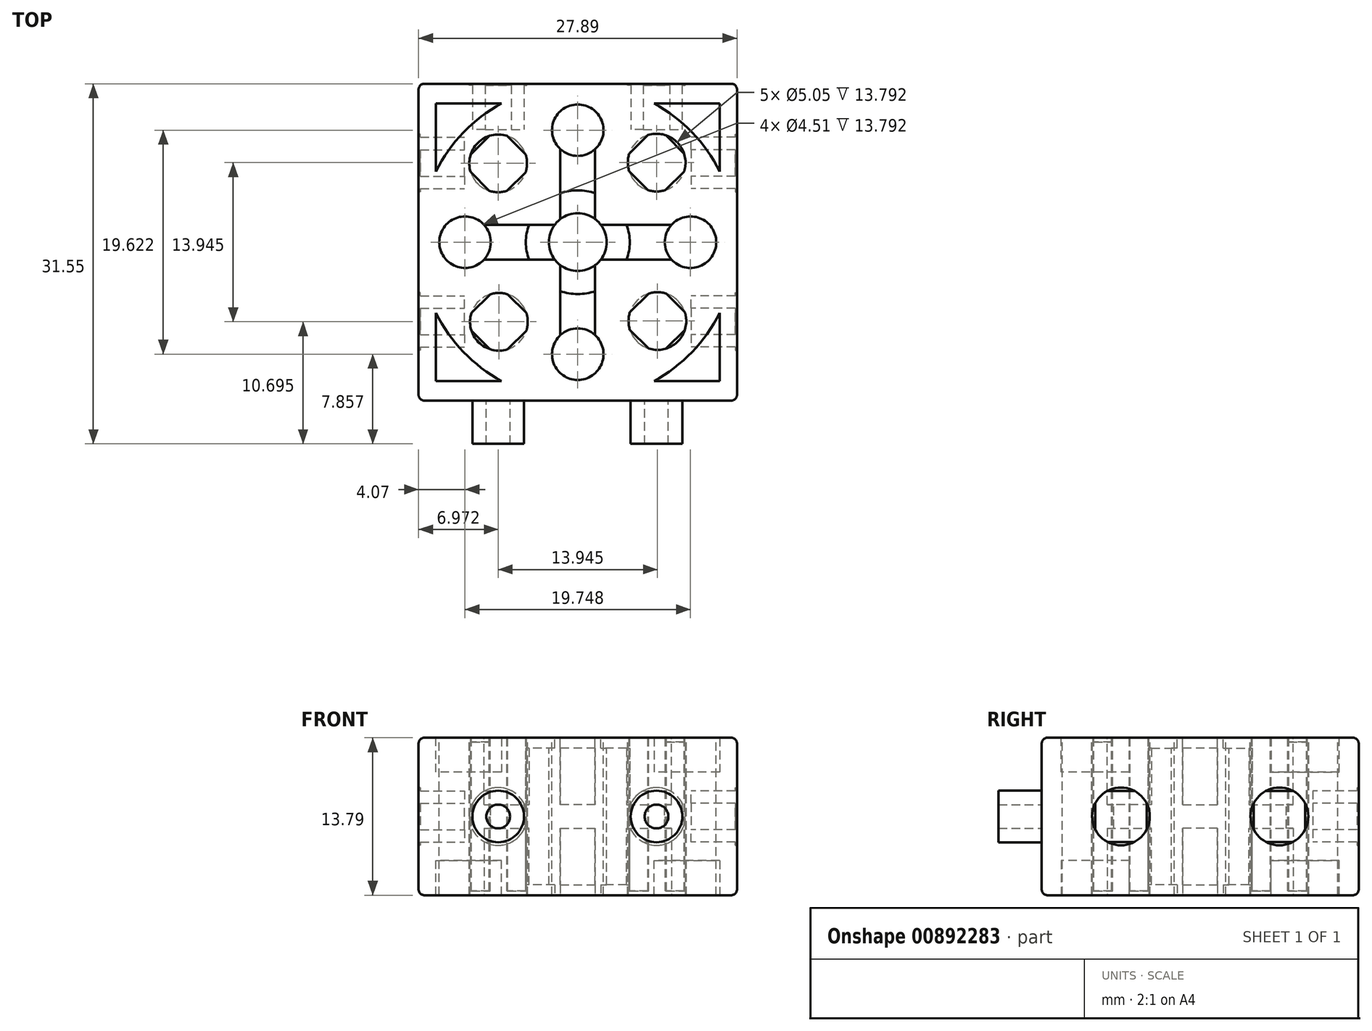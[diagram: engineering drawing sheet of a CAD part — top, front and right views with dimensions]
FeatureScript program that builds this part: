
annotation { "Feature Type Name" : "Feature", "Feature Type Description" : "" }
export const myFeature = defineFeature(function(context is Context, id is Id, definition is map)
    precondition{}
    {
        {
            var Q0;
            Q0=qCreatedBy(makeId("Top.planeOp"),FACE);
            var sketch = newSketch(context, id + "F0", { "sketchPlane" : qUnion([Q0])});
            skLineSegment(sketch, "E0.bottom", {"start": v(-12.61, 9.27) * mm, "end": v(15.28, 9.27) * mm});
            skLineSegment(sketch, "E0.top", {"start": v(-12.61, -18.5) * mm, "end": v(15.28, -18.5) * mm});
            skLineSegment(sketch, "E0.left", {"start": v(-12.61, 9.27) * mm, "end": v(-12.61, -18.5) * mm});
            skLineSegment(sketch, "E0.right", {"start": v(15.28, 9.27) * mm, "end": v(15.28, -18.5) * mm});
            skSolve(sketch);
        }
        {
            var Q0;
            Q0 = qSketchRegion(id + "F0", true);
            extrude(context, id + "F1", {"entities" : qUnion([Q0]), "depth" : 13.8 * mm, "offsetDistance" : 25.4 * mm});
        }
        {
            var Q0;
            Q0=makeQuery(id+"F1.opExtrude","CAP_FACE",FACE,{"disambiguationData":[OSD([sQuery(id+"F0.wireOp",EDGE,"E0.bottom"),sQuery(id+"F0.wireOp",EDGE,"E0.top"),sQuery(id+"F0.wireOp",EDGE,"E0.left"),sQuery(id+"F0.wireOp",EDGE,"E0.right")])],"isStart":false});
            var sketch = newSketch(context, id + "F2", { "sketchPlane" : qUnion([Q0])});
            skLineSegment(sketch, "E1", {"start": v(1.33, 9.27) * mm, "end": v(1.33, -18.5) * mm, "construction": true});
            skLineSegment(sketch, "E2", {"start": v(-12.61, -4.61) * mm, "end": v(15.28, -4.61) * mm, "construction": true});
            skLineSegment(sketch, "E3.bottom", {"start": v(13.75, 7.56) * mm, "end": v(-11.09, 7.56) * mm});
            skLineSegment(sketch, "E3.top", {"start": v(13.75, -16.78) * mm, "end": v(-11.09, -16.78) * mm});
            skLineSegment(sketch, "E3.left", {"start": v(13.75, 7.56) * mm, "end": v(13.75, -16.78) * mm});
            skLineSegment(sketch, "E3.right", {"start": v(-11.09, 7.56) * mm, "end": v(-11.09, -16.78) * mm});
            skPoint(sketch, "E3.middle", {"position": v(1.33, -4.61) * mm});
            skSolve(sketch);
        }
        {
            var Q0;
            Q0 = qSketchRegion(id + "F2", true);
            extrude(context, id + "F3", {"entities" : qUnion([Q0]), "operationType" : NewBodyOperationType.REMOVE, "oppositeDirection" : true, "depth" : 3.02 * mm, "offsetDistance" : 25.4 * mm});
        }
        {
            var Q0;
            Q0=makeQuery(id+"F1.opExtrude","CAP_FACE",FACE,{"disambiguationData":[OSD([sQuery(id+"F0.wireOp",EDGE,"E0.bottom"),sQuery(id+"F0.wireOp",EDGE,"E0.top"),sQuery(id+"F0.wireOp",EDGE,"E0.left"),sQuery(id+"F0.wireOp",EDGE,"E0.right")])],"isStart":true});
            var sketch = newSketch(context, id + "F4", { "sketchPlane" : qUnion([Q0])});
            skLineSegment(sketch, "E4.bottom", {"start": v(-11.09, -7.56) * mm, "end": v(13.75, -7.56) * mm});
            skLineSegment(sketch, "E4.top", {"start": v(-11.09, 16.78) * mm, "end": v(13.75, 16.78) * mm});
            skLineSegment(sketch, "E4.left", {"start": v(-11.09, -7.56) * mm, "end": v(-11.09, 16.78) * mm});
            skLineSegment(sketch, "E4.right", {"start": v(13.75, -7.56) * mm, "end": v(13.75, 16.78) * mm});
            skSolve(sketch);
        }
        {
            var Q0;
            Q0=makeQuery(id+"F4.imprint","IMPRINT",FACE,{"disambiguationData":[TD([[makeQuery(id+"F4.imprint","IMPRINT",EDGE,{"derivedFrom":sQuery(id+"F4.wireOp",EDGE,"E4.bottom")}),1.0]])]});
            extrude(context, id + "F5", {"entities" : qUnion([Q0]), "operationType" : NewBodyOperationType.REMOVE, "oppositeDirection" : true, "depth" : 3.02 * mm, "offsetDistance" : 25.4 * mm});
        }
        {
            var Q0;
            Q0=makeQuery(id+"F5.boolean.opBoolean","COPY",FACE,{"derivedFrom":makeQuery(id+"F5.opExtrude","CAP_FACE",FACE,{"disambiguationData":[OSD([sQuery(id+"F4.wireOp",EDGE,"E4.bottom"),sQuery(id+"F4.wireOp",EDGE,"E4.top"),sQuery(id+"F4.wireOp",EDGE,"E4.left"),sQuery(id+"F4.wireOp",EDGE,"E4.right")])],"isStart":false})});
            var sketch = newSketch(context, id + "F6", { "sketchPlane" : qUnion([Q0])});
            skCircle(sketch, "E5", {"center": v(1.33, 4.61) * mm, "radius": 13.88 * mm});
            skLineSegment(sketch, "E6", {"start": v(1.33, -7.56) * mm, "end": v(1.33, 16.78) * mm, "construction": true});
            skPoint(sketch, "E6.startSnap0", {"position": v(1.33, -7.56) * mm});
            skSolve(sketch);
        }
        {
            var Q0;
            {var subQ0=sQuery(id+"F6.wireOp",EDGE,"E5");var subQ1=makeQuery(id+"F5.boolean.opBoolean","COPY",EDGE,{"derivedFrom":makeQuery(id+"F5.opExtrude","CAP_EDGE",EDGE,{"disambiguationData":[OSD([sQuery(id+"F4.wireOp",EDGE,"E4.top")])],"isStart":false})});var subQ2=makeQuery(id+"F6.imprint","INTERSECT",VERTEX,{"disambiguationData":[OD(0.0)],"derivedFrom":[subQ1,subQ0]});Q0=makeQuery(id+"F6.imprint","IMPRINT",FACE,{"disambiguationData":[TD([[makeQuery(id+"F6.imprint","IMPRINT",EDGE,{"disambiguationData":[TD([[subQ2,-1.0]])],"derivedFrom":subQ0}),1.0]])]});}
            var Q1;
            {var subQ0=sQuery(id+"F6.wireOp",EDGE,"E5");var subQ1=makeQuery(id+"F5.boolean.opBoolean","COPY",EDGE,{"derivedFrom":makeQuery(id+"F5.opExtrude","CAP_EDGE",EDGE,{"disambiguationData":[OSD([sQuery(id+"F4.wireOp",EDGE,"E4.left")])],"isStart":false})});var subQ2=makeQuery(id+"F6.imprint","INTERSECT",VERTEX,{"disambiguationData":[OD(0.0)],"derivedFrom":[subQ1,subQ0]});Q1=makeQuery(id+"F6.imprint","IMPRINT",FACE,{"disambiguationData":[TD([[makeQuery(id+"F6.imprint","IMPRINT",EDGE,{"disambiguationData":[TD([[subQ2,-1.0]])],"derivedFrom":subQ0}),1.0]])]});}
            var Q2;
            {var subQ0=sQuery(id+"F6.wireOp",EDGE,"E5");var subQ1=makeQuery(id+"F5.boolean.opBoolean","COPY",EDGE,{"derivedFrom":makeQuery(id+"F5.opExtrude","CAP_EDGE",EDGE,{"disambiguationData":[OSD([sQuery(id+"F4.wireOp",EDGE,"E4.bottom")])],"isStart":false})});var subQ2=makeQuery(id+"F6.imprint","INTERSECT",VERTEX,{"disambiguationData":[OD(0.0)],"derivedFrom":[subQ1,subQ0]});Q2=makeQuery(id+"F6.imprint","IMPRINT",FACE,{"disambiguationData":[TD([[makeQuery(id+"F6.imprint","IMPRINT",EDGE,{"disambiguationData":[TD([[subQ2,-1.0]])],"derivedFrom":subQ0}),1.0]])]});}
            var Q3;
            {var subQ0=sQuery(id+"F6.wireOp",EDGE,"E5");var subQ1=makeQuery(id+"F5.boolean.opBoolean","COPY",EDGE,{"derivedFrom":makeQuery(id+"F5.opExtrude","CAP_EDGE",EDGE,{"disambiguationData":[OSD([sQuery(id+"F4.wireOp",EDGE,"E4.right")])],"isStart":false})});var subQ2=makeQuery(id+"F6.imprint","INTERSECT",VERTEX,{"disambiguationData":[OD(0.0)],"derivedFrom":[subQ1,subQ0]});Q3=makeQuery(id+"F6.imprint","IMPRINT",FACE,{"disambiguationData":[TD([[makeQuery(id+"F6.imprint","IMPRINT",EDGE,{"disambiguationData":[TD([[subQ2,1.0]])],"derivedFrom":subQ0}),1.0]])]});}
            var Q4;
            {var subQ0=sQuery(id+"F6.wireOp",EDGE,"E5");var subQ8=makeQuery(id+"F5.boolean.opBoolean","COPY",EDGE,{"derivedFrom":makeQuery(id+"F5.opExtrude","CAP_EDGE",EDGE,{"disambiguationData":[OSD([sQuery(id+"F4.wireOp",EDGE,"E4.top")])],"isStart":false})});var subQ11=makeQuery(id+"F6.imprint","INTERSECT",VERTEX,{"disambiguationData":[OD(0.0)],"derivedFrom":[subQ8,subQ0]});Q4=makeQuery(id+"F6.imprint","IMPRINT",FACE,{"disambiguationData":[TD([[makeQuery(id+"F6.imprint","IMPRINT",EDGE,{"disambiguationData":[TD([[subQ11,1.0]])],"derivedFrom":subQ0}),1.0]])]});}
            extrude(context, id + "F7", {"entities" : qUnion([Q0, Q1, Q2, Q3, Q4]), "operationType" : NewBodyOperationType.ADD, "depth" : 3.02 * mm, "offsetDistance" : 25.4 * mm});
        }
        {
            var Q0;
            Q0=makeQuery(id+"F3.boolean.opBoolean","COPY",FACE,{"derivedFrom":makeQuery(id+"F3.opExtrude","CAP_FACE",FACE,{"disambiguationData":[OSD([sQuery(id+"F2.wireOp",EDGE,"E3.bottom"),sQuery(id+"F2.wireOp",EDGE,"E3.top"),sQuery(id+"F2.wireOp",EDGE,"E3.left"),sQuery(id+"F2.wireOp",EDGE,"E3.right")])],"isStart":false})});
            var sketch = newSketch(context, id + "F8", { "sketchPlane" : qUnion([Q0])});
            skLineSegment(sketch, "E7", {"start": v(1.33, 7.56) * mm, "end": v(1.33, -16.78) * mm, "construction": true});
            skCircle(sketch, "E8", {"center": v(1.33, -4.61) * mm, "radius": 13.88 * mm});
            skSolve(sketch);
        }
        {
            var Q0;
            Q0 = qSketchRegion(id + "F8", true);
            extrude(context, id + "F9", {"entities" : qUnion([Q0]), "operationType" : NewBodyOperationType.ADD, "depth" : 3.02 * mm, "offsetDistance" : 25.4 * mm});
        }
        {
            var Q0;
            Q0=makeQuery(id+"F9.boolean.opBoolean","MERGE",FACE,{"derivedFrom":[makeQuery(id+"F1.opExtrude","CAP_FACE",FACE,{"disambiguationData":[OSD([sQuery(id+"F0.wireOp",EDGE,"E0.bottom"),sQuery(id+"F0.wireOp",EDGE,"E0.top"),sQuery(id+"F0.wireOp",EDGE,"E0.left"),sQuery(id+"F0.wireOp",EDGE,"E0.right")])],"isStart":false}),makeQuery(id+"F9.opExtrude","CAP_FACE",FACE,{"disambiguationData":[OSD([sQuery(id+"F8.wireOp",EDGE,"E8")])],"isStart":false})]});
            var sketch = newSketch(context, id + "F10", { "sketchPlane" : qUnion([Q0])});
            skLineSegment(sketch, "E9", {"start": v(-12.61, -4.61) * mm, "end": v(15.28, -4.61) * mm, "construction": true});
            skLineSegment(sketch, "E10", {"start": v(1.33, 9.27) * mm, "end": v(1.33, -18.5) * mm, "construction": true});
            skCircle(sketch, "E11", {"center": v(1.33, -4.61) * mm, "radius": 2.53 * mm});
            skCircle(sketch, "E12", {"center": v(1.33, -14.42) * mm, "radius": 2.25 * mm});
            skCircle(sketch, "E13", {"center": v(1.33, 5.2) * mm, "radius": 2.25 * mm});
            skCircle(sketch, "E14", {"center": v(-8.54, -4.61) * mm, "radius": 2.25 * mm});
            skCircle(sketch, "E15", {"center": v(11.2, -4.61) * mm, "radius": 2.25 * mm});
            skCircle(sketch, "E16", {"center": v(-5.64, 2.3) * mm, "radius": 2.53 * mm});
            skCircle(sketch, "E17.1.0", {"center": v(-5.57, -11.58) * mm, "radius": 2.53 * mm});
            skCircle(sketch, "E17.2.0", {"center": v(8.3, -11.52) * mm, "radius": 2.53 * mm});
            skCircle(sketch, "E17.3.0", {"center": v(8.24, 2.36) * mm, "radius": 2.53 * mm});
            skSolve(sketch);
        }
        {
            var Q0;
            Q0 = qSketchRegion(id + "F10", true);
            extrude(context, id + "F11", {"entities" : qUnion([Q0]), "operationType" : NewBodyOperationType.REMOVE, "oppositeDirection" : true, "depth" : 25.4 * mm, "offsetDistance" : 25.4 * mm});
        }
        {
            var Q0;
            Q0=makeQuery(id+"F9.boolean.opBoolean","MERGE",FACE,{"derivedFrom":[makeQuery(id+"F1.opExtrude","CAP_FACE",FACE,{"disambiguationData":[OSD([sQuery(id+"F0.wireOp",EDGE,"E0.bottom"),sQuery(id+"F0.wireOp",EDGE,"E0.top"),sQuery(id+"F0.wireOp",EDGE,"E0.left"),sQuery(id+"F0.wireOp",EDGE,"E0.right")])],"isStart":false}),makeQuery(id+"F9.opExtrude","CAP_FACE",FACE,{"disambiguationData":[OSD([sQuery(id+"F8.wireOp",EDGE,"E8")])],"isStart":false})]});
            var sketch = newSketch(context, id + "F12", { "sketchPlane" : qUnion([Q0])});
            skLineSegment(sketch, "E18", {"start": v(-12.61, -4.61) * mm, "end": v(15.28, -4.61) * mm, "construction": true});
            skLineSegment(sketch, "E19", {"start": v(1.33, 9.27) * mm, "end": v(1.33, -18.5) * mm, "construction": true});
            skLineSegment(sketch, "E20", {"start": v(-6.88, -3.09) * mm, "end": v(9.55, -3.09) * mm});
            skLineSegment(sketch, "E21", {"start": v(-6.88, -6.14) * mm, "end": v(9.55, -6.14) * mm});
            skLineSegment(sketch, "E22", {"start": v(-0.19, 3.54) * mm, "end": v(-0.19, -12.76) * mm});
            skLineSegment(sketch, "E23", {"start": v(2.86, -12.76) * mm, "end": v(2.86, 3.54) * mm});
            skLineSegment(sketch, "E24", {"start": v(-0.19, -7.96) * mm, "end": v(2.86, -7.96) * mm, "construction": true});
            skPoint(sketch, "E25", {"position": v(1.33, -7.96) * mm});
            skLineSegment(sketch, "E26", {"start": v(-2, -3.09) * mm, "end": v(-2, -6.14) * mm, "construction": true});
            skPoint(sketch, "E27", {"position": v(-2, -4.61) * mm});
            skSolve(sketch);
        }
        {
            var Q0;
            {var subQ0=sQuery(id+"F12.wireOp",EDGE,"E22");var subQ1=makeQuery(id+"F11.boolean.opBoolean","COPY",EDGE,{"derivedFrom":makeQuery(id+"F11.opExtrude","CAP_EDGE",EDGE,{"disambiguationData":[OSD([sQuery(id+"F10.wireOp",EDGE,"E13")])],"isStart":true})});var subQ2=makeQuery(id+"F12.imprint","INTERSECT",VERTEX,{"derivedFrom":[subQ1,subQ0]});Q0=makeQuery(id+"F12.imprint","IMPRINT",FACE,{"disambiguationData":[TD([[makeQuery(id+"F12.imprint","IMPRINT",EDGE,{"disambiguationData":[TD([[subQ2,-1.0]])],"derivedFrom":subQ0}),1.0]])]});}
            var Q1;
            {var subQ0=sQuery(id+"F12.wireOp",EDGE,"E22");var subQ1=makeQuery(id+"F11.boolean.opBoolean","COPY",EDGE,{"derivedFrom":makeQuery(id+"F11.opExtrude","CAP_EDGE",EDGE,{"disambiguationData":[OSD([sQuery(id+"F10.wireOp",EDGE,"E12")])],"isStart":true})});var subQ2=makeQuery(id+"F12.imprint","INTERSECT",VERTEX,{"derivedFrom":[subQ1,subQ0]});Q1=makeQuery(id+"F12.imprint","IMPRINT",FACE,{"disambiguationData":[TD([[makeQuery(id+"F12.imprint","IMPRINT",EDGE,{"disambiguationData":[TD([[subQ2,1.0]])],"derivedFrom":subQ0}),1.0]])]});}
            var Q2;
            {var subQ0=sQuery(id+"F12.wireOp",EDGE,"E20");var subQ1=makeQuery(id+"F11.boolean.opBoolean","COPY",EDGE,{"derivedFrom":makeQuery(id+"F11.opExtrude","CAP_EDGE",EDGE,{"disambiguationData":[OSD([sQuery(id+"F10.wireOp",EDGE,"E14")])],"isStart":true})});var subQ2=makeQuery(id+"F12.imprint","INTERSECT",VERTEX,{"derivedFrom":[subQ1,subQ0]});Q2=makeQuery(id+"F12.imprint","IMPRINT",FACE,{"disambiguationData":[TD([[makeQuery(id+"F12.imprint","IMPRINT",EDGE,{"disambiguationData":[TD([[subQ2,-1.0]])],"derivedFrom":subQ0}),-1.0]])]});}
            var Q3;
            {var subQ0=sQuery(id+"F12.wireOp",EDGE,"E20");var subQ1=makeQuery(id+"F11.boolean.opBoolean","COPY",EDGE,{"derivedFrom":makeQuery(id+"F11.opExtrude","CAP_EDGE",EDGE,{"disambiguationData":[OSD([sQuery(id+"F10.wireOp",EDGE,"E15")])],"isStart":true})});var subQ2=makeQuery(id+"F12.imprint","INTERSECT",VERTEX,{"derivedFrom":[subQ1,subQ0]});Q3=makeQuery(id+"F12.imprint","IMPRINT",FACE,{"disambiguationData":[TD([[makeQuery(id+"F12.imprint","IMPRINT",EDGE,{"disambiguationData":[TD([[subQ2,1.0]])],"derivedFrom":subQ0}),-1.0]])]});}
            extrude(context, id + "F13", {"entities" : qUnion([Q0, Q1, Q2, Q3]), "operationType" : NewBodyOperationType.REMOVE, "oppositeDirection" : true, "depth" : 5.87 * mm, "offsetDistance" : 25.4 * mm});
        }
        {
            var Q0;
            Q0=makeQuery(id+"F7.boolean.opBoolean","MERGE",FACE,{"derivedFrom":[makeQuery(id+"F1.opExtrude","CAP_FACE",FACE,{"disambiguationData":[OSD([sQuery(id+"F0.wireOp",EDGE,"E0.bottom"),sQuery(id+"F0.wireOp",EDGE,"E0.top"),sQuery(id+"F0.wireOp",EDGE,"E0.left"),sQuery(id+"F0.wireOp",EDGE,"E0.right")])],"isStart":true}),makeQuery(id+"F7.opExtrude","CAP_FACE",FACE,{"disambiguationData":[OSD([sQuery(id+"F6.wireOp",EDGE,"E5")])],"isStart":false})]});
            var sketch = newSketch(context, id + "F14", { "sketchPlane" : qUnion([Q0])});
            skLineSegment(sketch, "E28.0", {"start": v(2.86, 12.76) * mm, "end": v(2.86, 6.63) * mm});
            skLineSegment(sketch, "E28.1", {"start": v(3.35, 6.14) * mm, "end": v(9.55, 6.14) * mm});
            skLineSegment(sketch, "E28.2", {"start": v(3.35, 3.09) * mm, "end": v(9.55, 3.09) * mm});
            skLineSegment(sketch, "E28.3", {"start": v(2.86, 2.6) * mm, "end": v(2.86, -3.54) * mm});
            skLineSegment(sketch, "E28.4", {"start": v(-0.19, -3.54) * mm, "end": v(-0.19, 2.6) * mm});
            skLineSegment(sketch, "E28.5", {"start": v(-0.19, 6.63) * mm, "end": v(-0.19, 12.76) * mm});
            skLineSegment(sketch, "E28.6", {"start": v(-6.88, 6.14) * mm, "end": v(-0.68, 6.14) * mm});
            skLineSegment(sketch, "E28.7", {"start": v(-6.88, 3.09) * mm, "end": v(-0.68, 3.09) * mm});
            skSolve(sketch);
        }
        {
            var Q0;
            {var subQ0=sQuery(id+"F14.wireOp",EDGE,"E28.6");Q0=makeQuery(id+"F14.imprint","IMPRINT",FACE,{"disambiguationData":[TD([[makeQuery(id+"F14.imprint","IMPRINT",EDGE,{"derivedFrom":subQ0}),-1.0]])]});}
            var Q1;
            {var subQ0=sQuery(id+"F14.wireOp",EDGE,"E28.3");Q1=makeQuery(id+"F14.imprint","IMPRINT",FACE,{"disambiguationData":[TD([[makeQuery(id+"F14.imprint","IMPRINT",EDGE,{"derivedFrom":subQ0}),-1.0]])]});}
            var Q2;
            {var subQ0=sQuery(id+"F14.wireOp",EDGE,"E28.0");Q2=makeQuery(id+"F14.imprint","IMPRINT",FACE,{"disambiguationData":[TD([[makeQuery(id+"F14.imprint","IMPRINT",EDGE,{"derivedFrom":subQ0}),-1.0]])]});}
            var Q3;
            {var subQ0=sQuery(id+"F14.wireOp",EDGE,"E28.1");Q3=makeQuery(id+"F14.imprint","IMPRINT",FACE,{"disambiguationData":[TD([[makeQuery(id+"F14.imprint","IMPRINT",EDGE,{"derivedFrom":subQ0}),-1.0]])]});}
            extrude(context, id + "F15", {"entities" : qUnion([Q0, Q1, Q2, Q3]), "operationType" : NewBodyOperationType.REMOVE, "oppositeDirection" : true, "depth" : 5.87 * mm, "offsetDistance" : 25.4 * mm});
        }
        {
            var Q0;
            Q0=makeQuery(id+"F15.boolean.opBoolean","COPY",FACE,{"derivedFrom":makeQuery(id+"F15.opExtrude","CAP_FACE",FACE,{"disambiguationData":[OSD([sQuery(id+"F0.wireOp",EDGE,"E0.bottom"),sQuery(id+"F0.wireOp",EDGE,"E0.top"),sQuery(id+"F0.wireOp",EDGE,"E0.left"),sQuery(id+"F0.wireOp",EDGE,"E0.right"),sQuery(id+"F6.wireOp",EDGE,"E5"),sQuery(id+"F10.wireOp",EDGE,"E11"),sQuery(id+"F10.wireOp",EDGE,"E13"),sQuery(id+"F14.wireOp",EDGE,"E28.3"),sQuery(id+"F14.wireOp",EDGE,"E28.4")])],"isStart":false})});
            var sketch = newSketch(context, id + "F16", { "sketchPlane" : qUnion([Q0])});
            skCircle(sketch, "E29", {"center": v(1.33, 4.61) * mm, "radius": 4.55 * mm});
            skCircle(sketch, "E30", {"center": v(1.33, 4.61) * mm, "radius": 2.53 * mm});
            skSolve(sketch);
        }
        {
            var Q0;
            {var subQ5=sQuery(id+"F16.wireOp",EDGE,"E30");Q0=makeQuery(id+"F16.imprint","IMPRINT",FACE,{"disambiguationData":[TD([[makeQuery(id+"F16.imprint","IMPRINT",EDGE,{"disambiguationData":[OD(1.0)],"derivedFrom":subQ5}),-1.0]])]});}
            var Q1;
            {var subQ5=sQuery(id+"F16.wireOp",EDGE,"E30");Q1=makeQuery(id+"F16.imprint","IMPRINT",FACE,{"disambiguationData":[TD([[makeQuery(id+"F16.imprint","IMPRINT",EDGE,{"disambiguationData":[OD(0.0)],"derivedFrom":subQ5}),1.0]])]});}
            extrude(context, id + "F17", {"entities" : qUnion([Q0, Q1]), "operationType" : NewBodyOperationType.ADD, "depth" : 4.95 * mm, "offsetDistance" : 25.4 * mm});
        }
        {
            var Q0;
            Q0=makeQuery(id+"F13.boolean.opBoolean","COPY",FACE,{"derivedFrom":makeQuery(id+"F13.opExtrude","CAP_FACE",FACE,{"disambiguationData":[OSD([sQuery(id+"F10.wireOp",EDGE,"E11"),sQuery(id+"F10.wireOp",EDGE,"E12"),sQuery(id+"F12.wireOp",EDGE,"E22"),sQuery(id+"F12.wireOp",EDGE,"E23")])],"isStart":false})});
            var sketch = newSketch(context, id + "F18", { "sketchPlane" : qUnion([Q0])});
            skCircle(sketch, "E31", {"center": v(1.33, -4.61) * mm, "radius": 4.55 * mm});
            skCircle(sketch, "E32", {"center": v(1.33, -4.61) * mm, "radius": 2.53 * mm});
            skSolve(sketch);
        }
        {
            var Q0;
            {var subQ0=sQuery(id+"F18.wireOp",EDGE,"E31");var subQ1=sQuery(id+"F12.wireOp",EDGE,"E22");var subQ2=makeQuery(id+"F11.boolean.opBoolean","COPY",EDGE,{"derivedFrom":makeQuery(id+"F11.opExtrude","CAP_EDGE",EDGE,{"disambiguationData":[OSD([sQuery(id+"F10.wireOp",EDGE,"E12")])],"isStart":true})});var subQ4=makeQuery(id+"F13.boolean.opBoolean","COPY",EDGE,{"derivedFrom":makeQuery(id+"F13.opExtrude","CAP_EDGE",EDGE,{"disambiguationData":[OSD([subQ1]),TDD([makeQuery(id+"F12.imprint","IMPRINT",EDGE,{"disambiguationData":[TD([[makeQuery(id+"F12.imprint","INTERSECT",VERTEX,{"derivedFrom":[subQ2,subQ1]}),1.0]])],"derivedFrom":subQ1})])],"isStart":false})});var subQ5=makeQuery(id+"F18.imprint","INTERSECT",VERTEX,{"derivedFrom":[subQ4,subQ0]});Q0=makeQuery(id+"F18.imprint","IMPRINT",FACE,{"disambiguationData":[TD([[makeQuery(id+"F18.imprint","IMPRINT",EDGE,{"disambiguationData":[TD([[subQ5,1.0]])],"derivedFrom":subQ0}),1.0]])]});}
            var Q1;
            {var subQ0=sQuery(id+"F18.wireOp",EDGE,"E31");var subQ1=sQuery(id+"F12.wireOp",EDGE,"E22");var subQ2=makeQuery(id+"F11.boolean.opBoolean","COPY",EDGE,{"derivedFrom":makeQuery(id+"F11.opExtrude","CAP_EDGE",EDGE,{"disambiguationData":[OSD([sQuery(id+"F10.wireOp",EDGE,"E12")])],"isStart":true})});var subQ4=makeQuery(id+"F13.boolean.opBoolean","COPY",EDGE,{"derivedFrom":makeQuery(id+"F13.opExtrude","CAP_EDGE",EDGE,{"disambiguationData":[OSD([subQ1]),TDD([makeQuery(id+"F12.imprint","IMPRINT",EDGE,{"disambiguationData":[TD([[makeQuery(id+"F12.imprint","INTERSECT",VERTEX,{"derivedFrom":[subQ2,subQ1]}),1.0]])],"derivedFrom":subQ1})])],"isStart":false})});var subQ5=makeQuery(id+"F18.imprint","INTERSECT",VERTEX,{"derivedFrom":[subQ4,subQ0]});Q1=makeQuery(id+"F18.imprint","IMPRINT",FACE,{"disambiguationData":[TD([[makeQuery(id+"F18.imprint","IMPRINT",EDGE,{"disambiguationData":[TD([[subQ5,-1.0]])],"derivedFrom":subQ0}),1.0]])]});}
            extrude(context, id + "F19", {"entities" : qUnion([Q0, Q1]), "operationType" : NewBodyOperationType.ADD, "depth" : 4.95 * mm, "offsetDistance" : 25.4 * mm});
        }
        {
            var Q0;
            Q0=makeQuery(id+"F1.opExtrude","SWEPT_FACE",FACE,{"disambiguationData":[OSD([sQuery(id+"F0.wireOp",EDGE,"E0.top")])]});
            var sketch = newSketch(context, id + "F20", { "sketchPlane" : qUnion([Q0])});
            skLineSegment(sketch, "E33", {"start": v(15.28, 6.9) * mm, "end": v(-12.61, 6.9) * mm, "construction": true});
            skCircle(sketch, "E34", {"center": v(8.23, 6.9) * mm, "radius": 2.26 * mm});
            skCircle(sketch, "E35", {"center": v(-5.64, 6.9) * mm, "radius": 2.26 * mm});
            skLineSegment(sketch, "E36", {"start": v(1.33, 0) * mm, "end": v(1.33, 13.8) * mm, "construction": true});
            skPoint(sketch, "E37", {"position": v(1.33, 6.9) * mm});
            skLineSegment(sketch, "E38", {"start": v(1.33, 0) * mm, "end": v(15.28, 0) * mm, "construction": true});
            skLineSegment(sketch, "E39", {"start": v(15.28, 0) * mm, "end": v(8.3, 0) * mm});
            skLineSegment(sketch, "E40", {"start": v(8.3, 0) * mm, "end": v(8.3, 13.8) * mm, "construction": true});
            skLineSegment(sketch, "E41", {"start": v(1.33, 0) * mm, "end": v(-12.61, 0) * mm, "construction": true});
            skLineSegment(sketch, "E42", {"start": v(-5.64, 0) * mm, "end": v(-5.64, 13.8) * mm, "construction": true});
            skCircle(sketch, "E43", {"center": v(8.23, 6.9) * mm, "radius": 1.04 * mm});
            skCircle(sketch, "E44", {"center": v(-5.64, 6.9) * mm, "radius": 1.04 * mm});
            skLineSegment(sketch, "E45.0", {"start": v(-12.61, 13.8) * mm, "end": v(-12.61, 0) * mm});
            skSolve(sketch);
        }
        {
            var Q0;
            Q0=makeQuery(id+"F20.imprint","IMPRINT",FACE,{"disambiguationData":[TD([[makeQuery(id+"F20.imprint","IMPRINT",EDGE,{"derivedFrom":sQuery(id+"F20.wireOp",EDGE,"E34")}),1.0]])]});
            var Q1;
            Q1=makeQuery(id+"F20.imprint","IMPRINT",FACE,{"disambiguationData":[TD([[makeQuery(id+"F20.imprint","IMPRINT",EDGE,{"derivedFrom":sQuery(id+"F20.wireOp",EDGE,"E35")}),1.0]])]});
            extrude(context, id + "F21", {"entities" : qUnion([Q0, Q1]), "operationType" : NewBodyOperationType.ADD, "depth" : 3.78 * mm, "offsetDistance" : 25.4 * mm});
        }
        {
            var Q0;
            Q0=makeQuery(id+"F1.opExtrude","SWEPT_FACE",FACE,{"disambiguationData":[OSD([sQuery(id+"F0.wireOp",EDGE,"E0.bottom")])]});
            var sketch = newSketch(context, id + "F22", { "sketchPlane" : qUnion([Q0])});
            skCircle(sketch, "E46.0", {"center": v(-8.23, 6.9) * mm, "radius": 2.26 * mm, "construction": true});
            skCircle(sketch, "E46.1", {"center": v(5.64, 6.9) * mm, "radius": 2.26 * mm, "construction": true});
            skCircle(sketch, "E47", {"center": v(-8.23, 6.9) * mm, "radius": 2.53 * mm});
            skCircle(sketch, "E48", {"center": v(5.64, 6.9) * mm, "radius": 2.53 * mm});
            skSolve(sketch);
        }
        {
            var Q0;
            Q0 = qSketchRegion(id + "F22", true);
            extrude(context, id + "F23", {"entities" : qUnion([Q0]), "operationType" : NewBodyOperationType.REMOVE, "oppositeDirection" : true, "depth" : 4 * mm, "offsetDistance" : 25.4 * mm});
        }
        {
            var Q0;
            Q0=makeQuery(id+"F1.opExtrude","SWEPT_FACE",FACE,{"disambiguationData":[OSD([sQuery(id+"F0.wireOp",EDGE,"E0.right")])]});
            var sketch = newSketch(context, id + "F24", { "sketchPlane" : qUnion([Q0])});
            skLineSegment(sketch, "E49", {"start": v(9.27, 6.9) * mm, "end": v(-18.5, 6.9) * mm, "construction": true});
            skLineSegment(sketch, "E50", {"start": v(-4.61, 13.8) * mm, "end": v(-4.61, 0) * mm});
            skLineSegment(sketch, "E51", {"start": v(-4.61, 13.8) * mm, "end": v(9.27, 13.8) * mm, "construction": true});
            skLineSegment(sketch, "E52", {"start": v(-4.61, 13.8) * mm, "end": v(-18.5, 13.8) * mm, "construction": true});
            skLineSegment(sketch, "E53", {"start": v(-11.55, 13.8) * mm, "end": v(-11.55, 0) * mm, "construction": true});
            skLineSegment(sketch, "E54", {"start": v(2.33, 13.8) * mm, "end": v(2.33, 0) * mm, "construction": true});
            skPoint(sketch, "E55", {"position": v(-11.55, 6.9) * mm});
            skPoint(sketch, "E56", {"position": v(2.33, 6.9) * mm});
            skCircle(sketch, "E57", {"center": v(-11.55, 6.9) * mm, "radius": 2.53 * mm});
            skCircle(sketch, "E58", {"center": v(2.33, 6.9) * mm, "radius": 2.53 * mm});
            skSolve(sketch);
        }
        {
            var Q0;
            Q0 = qSketchRegion(id + "F24", true);
            extrude(context, id + "F25", {"entities" : qUnion([Q0]), "operationType" : NewBodyOperationType.REMOVE, "oppositeDirection" : true, "depth" : 4 * mm, "offsetDistance" : 25.4 * mm});
        }
        {
            var Q0;
            Q0=makeQuery(id+"F1.opExtrude","SWEPT_FACE",FACE,{"disambiguationData":[OSD([sQuery(id+"F0.wireOp",EDGE,"E0.left")])]});
            var sketch = newSketch(context, id + "F26", { "sketchPlane" : qUnion([Q0])});
            skCircle(sketch, "E59.0", {"center": v(-2.33, 6.9) * mm, "radius": 2.53 * mm});
            skCircle(sketch, "E59.1", {"center": v(11.55, 6.9) * mm, "radius": 2.53 * mm});
            skSolve(sketch);
        }
        {
            var Q0;
            Q0 = qSketchRegion(id + "F26", true);
            extrude(context, id + "F27", {"entities" : qUnion([Q0]), "operationType" : NewBodyOperationType.REMOVE, "oppositeDirection" : true, "depth" : 4 * mm, "offsetDistance" : 25.4 * mm});
        }
        {
            var Q0;
            Q0=makeQuery(id+"F23.boolean.opBoolean","COPY",FACE,{"derivedFrom":makeQuery(id+"F23.opExtrude","CAP_FACE",FACE,{"disambiguationData":[OSD([sQuery(id+"F22.wireOp",EDGE,"E47")])],"isStart":false})});
            var sketch = newSketch(context, id + "F28", { "sketchPlane" : qUnion([Q0])});
            skLineSegment(sketch, "E60.bottom", {"start": v(-5.98, 9.14) * mm, "end": v(-10.48, 9.14) * mm});
            skLineSegment(sketch, "E60.top", {"start": v(-5.98, 4.65) * mm, "end": v(-10.48, 4.65) * mm});
            skLineSegment(sketch, "E60.left", {"start": v(-5.98, 9.14) * mm, "end": v(-5.98, 4.65) * mm});
            skLineSegment(sketch, "E60.right", {"start": v(-10.48, 9.14) * mm, "end": v(-10.48, 4.65) * mm});
            skPoint(sketch, "E60.middle", {"position": v(-8.23, 6.9) * mm});
            skLineSegment(sketch, "E61.bottom", {"start": v(7.89, 9.14) * mm, "end": v(3.4, 9.14) * mm});
            skLineSegment(sketch, "E61.top", {"start": v(7.89, 4.65) * mm, "end": v(3.4, 4.65) * mm});
            skLineSegment(sketch, "E61.left", {"start": v(7.89, 9.14) * mm, "end": v(7.89, 4.65) * mm});
            skLineSegment(sketch, "E61.right", {"start": v(3.4, 9.14) * mm, "end": v(3.4, 4.65) * mm});
            skPoint(sketch, "E61.middle", {"position": v(5.64, 6.9) * mm});
            skCircle(sketch, "E62.0", {"center": v(-8.23, 6.9) * mm, "radius": 2.53 * mm});
            skCircle(sketch, "E63.0", {"center": v(5.64, 6.9) * mm, "radius": 2.53 * mm});
            skSolve(sketch);
        }
        {
            var Q0;
            {var subQ0=sQuery(id+"F28.wireOp",EDGE,"E62.0");var subQ1=sQuery(id+"F28.wireOp",EDGE,"E60.right");var subQ2=makeQuery(id+"F28.imprint","INTERSECT",VERTEX,{"disambiguationData":[OD(0.0)],"derivedFrom":[subQ1,subQ0]});Q0=makeQuery(id+"F28.imprint","IMPRINT",FACE,{"disambiguationData":[TD([[makeQuery(id+"F28.imprint","IMPRINT",EDGE,{"disambiguationData":[TD([[subQ2,-1.0]])],"derivedFrom":subQ1}),-1.0]])]});}
            var Q1;
            {var subQ0=sQuery(id+"F28.wireOp",EDGE,"E62.0");var subQ1=sQuery(id+"F28.wireOp",EDGE,"E60.top");var subQ2=makeQuery(id+"F28.imprint","INTERSECT",VERTEX,{"disambiguationData":[OD(0.0)],"derivedFrom":[subQ1,subQ0]});Q1=makeQuery(id+"F28.imprint","IMPRINT",FACE,{"disambiguationData":[TD([[makeQuery(id+"F28.imprint","IMPRINT",EDGE,{"disambiguationData":[TD([[subQ2,-1.0]])],"derivedFrom":subQ1}),1.0]])]});}
            var Q2;
            {var subQ0=sQuery(id+"F28.wireOp",EDGE,"E62.0");var subQ1=sQuery(id+"F28.wireOp",EDGE,"E60.left");var subQ2=makeQuery(id+"F28.imprint","INTERSECT",VERTEX,{"disambiguationData":[OD(0.0)],"derivedFrom":[subQ1,subQ0]});Q2=makeQuery(id+"F28.imprint","IMPRINT",FACE,{"disambiguationData":[TD([[makeQuery(id+"F28.imprint","IMPRINT",EDGE,{"disambiguationData":[TD([[subQ2,-1.0]])],"derivedFrom":subQ1}),1.0]])]});}
            var Q3;
            {var subQ0=sQuery(id+"F28.wireOp",EDGE,"E62.0");var subQ1=sQuery(id+"F28.wireOp",EDGE,"E60.bottom");var subQ2=makeQuery(id+"F28.imprint","INTERSECT",VERTEX,{"disambiguationData":[OD(0.0)],"derivedFrom":[subQ1,subQ0]});Q3=makeQuery(id+"F28.imprint","IMPRINT",FACE,{"disambiguationData":[TD([[makeQuery(id+"F28.imprint","IMPRINT",EDGE,{"disambiguationData":[TD([[subQ2,-1.0]])],"derivedFrom":subQ1}),-1.0]])]});}
            var Q4;
            {var subQ0=sQuery(id+"F28.wireOp",EDGE,"E63.0");var subQ1=sQuery(id+"F28.wireOp",EDGE,"E61.bottom");var subQ2=makeQuery(id+"F28.imprint","INTERSECT",VERTEX,{"disambiguationData":[OD(0.0)],"derivedFrom":[subQ1,subQ0]});Q4=makeQuery(id+"F28.imprint","IMPRINT",FACE,{"disambiguationData":[TD([[makeQuery(id+"F28.imprint","IMPRINT",EDGE,{"disambiguationData":[TD([[subQ2,-1.0]])],"derivedFrom":subQ1}),-1.0]])]});}
            var Q5;
            {var subQ0=sQuery(id+"F28.wireOp",EDGE,"E63.0");var subQ1=sQuery(id+"F28.wireOp",EDGE,"E61.left");var subQ2=makeQuery(id+"F28.imprint","INTERSECT",VERTEX,{"disambiguationData":[OD(0.0)],"derivedFrom":[subQ1,subQ0]});Q5=makeQuery(id+"F28.imprint","IMPRINT",FACE,{"disambiguationData":[TD([[makeQuery(id+"F28.imprint","IMPRINT",EDGE,{"disambiguationData":[TD([[subQ2,-1.0]])],"derivedFrom":subQ1}),1.0]])]});}
            var Q6;
            {var subQ0=sQuery(id+"F28.wireOp",EDGE,"E63.0");var subQ1=sQuery(id+"F28.wireOp",EDGE,"E61.right");var subQ2=makeQuery(id+"F28.imprint","INTERSECT",VERTEX,{"disambiguationData":[OD(0.0)],"derivedFrom":[subQ1,subQ0]});Q6=makeQuery(id+"F28.imprint","IMPRINT",FACE,{"disambiguationData":[TD([[makeQuery(id+"F28.imprint","IMPRINT",EDGE,{"disambiguationData":[TD([[subQ2,-1.0]])],"derivedFrom":subQ1}),-1.0]])]});}
            var Q7;
            {var subQ0=sQuery(id+"F28.wireOp",EDGE,"E63.0");var subQ1=sQuery(id+"F28.wireOp",EDGE,"E61.top");var subQ2=makeQuery(id+"F28.imprint","INTERSECT",VERTEX,{"disambiguationData":[OD(0.0)],"derivedFrom":[subQ1,subQ0]});Q7=makeQuery(id+"F28.imprint","IMPRINT",FACE,{"disambiguationData":[TD([[makeQuery(id+"F28.imprint","IMPRINT",EDGE,{"disambiguationData":[TD([[subQ2,-1.0]])],"derivedFrom":subQ1}),1.0]])]});}
            extrude(context, id + "F29", {"entities" : qUnion([Q0, Q1, Q2, Q3, Q4, Q5, Q6, Q7]), "operationType" : NewBodyOperationType.ADD, "depth" : 3.86 * mm, "offsetDistance" : 25.4 * mm});
        }
        {
            var Q0;
            Q0=makeQuery(id+"F25.boolean.opBoolean","COPY",FACE,{"derivedFrom":makeQuery(id+"F25.opExtrude","CAP_FACE",FACE,{"disambiguationData":[OSD([sQuery(id+"F24.wireOp",EDGE,"E57")])],"isStart":false})});
            var sketch = newSketch(context, id + "F30", { "sketchPlane" : qUnion([Q0])});
            skLineSegment(sketch, "E64.bottom", {"start": v(-9.3, 9.14) * mm, "end": v(-13.8, 9.14) * mm});
            skLineSegment(sketch, "E64.top", {"start": v(-9.3, 4.65) * mm, "end": v(-13.8, 4.65) * mm});
            skLineSegment(sketch, "E64.left", {"start": v(-9.3, 9.14) * mm, "end": v(-9.3, 4.65) * mm});
            skLineSegment(sketch, "E64.right", {"start": v(-13.8, 9.14) * mm, "end": v(-13.8, 4.65) * mm});
            skPoint(sketch, "E64.middle", {"position": v(-11.55, 6.9) * mm});
            skLineSegment(sketch, "E65.bottom", {"start": v(4.58, 9.14) * mm, "end": v(0.08, 9.14) * mm});
            skLineSegment(sketch, "E65.top", {"start": v(4.58, 4.65) * mm, "end": v(0.08, 4.65) * mm});
            skLineSegment(sketch, "E65.left", {"start": v(4.58, 9.14) * mm, "end": v(4.58, 4.65) * mm});
            skLineSegment(sketch, "E65.right", {"start": v(0.08, 9.14) * mm, "end": v(0.08, 4.65) * mm});
            skPoint(sketch, "E65.middle", {"position": v(2.33, 6.9) * mm});
            skCircle(sketch, "E66.0", {"center": v(-11.55, 6.9) * mm, "radius": 2.53 * mm});
            skCircle(sketch, "E66.1", {"center": v(2.33, 6.9) * mm, "radius": 2.53 * mm});
            skSolve(sketch);
        }
        {
            var Q0;
            {var subQ0=sQuery(id+"F30.wireOp",EDGE,"E66.0");var subQ1=sQuery(id+"F30.wireOp",EDGE,"E64.bottom");var subQ2=makeQuery(id+"F30.imprint","INTERSECT",VERTEX,{"disambiguationData":[OD(0.0)],"derivedFrom":[subQ1,subQ0]});Q0=makeQuery(id+"F30.imprint","IMPRINT",FACE,{"disambiguationData":[TD([[makeQuery(id+"F30.imprint","IMPRINT",EDGE,{"disambiguationData":[TD([[subQ2,-1.0]])],"derivedFrom":subQ1}),-1.0]])]});}
            var Q1;
            {var subQ0=sQuery(id+"F30.wireOp",EDGE,"E66.0");var subQ1=sQuery(id+"F30.wireOp",EDGE,"E64.right");var subQ2=makeQuery(id+"F30.imprint","INTERSECT",VERTEX,{"disambiguationData":[OD(0.0)],"derivedFrom":[subQ1,subQ0]});Q1=makeQuery(id+"F30.imprint","IMPRINT",FACE,{"disambiguationData":[TD([[makeQuery(id+"F30.imprint","IMPRINT",EDGE,{"disambiguationData":[TD([[subQ2,-1.0]])],"derivedFrom":subQ1}),-1.0]])]});}
            var Q2;
            {var subQ0=sQuery(id+"F30.wireOp",EDGE,"E66.0");var subQ1=sQuery(id+"F30.wireOp",EDGE,"E64.left");var subQ2=makeQuery(id+"F30.imprint","INTERSECT",VERTEX,{"disambiguationData":[OD(0.0)],"derivedFrom":[subQ1,subQ0]});Q2=makeQuery(id+"F30.imprint","IMPRINT",FACE,{"disambiguationData":[TD([[makeQuery(id+"F30.imprint","IMPRINT",EDGE,{"disambiguationData":[TD([[subQ2,-1.0]])],"derivedFrom":subQ1}),1.0]])]});}
            var Q3;
            {var subQ0=sQuery(id+"F30.wireOp",EDGE,"E66.0");var subQ1=sQuery(id+"F30.wireOp",EDGE,"E64.top");var subQ2=makeQuery(id+"F30.imprint","INTERSECT",VERTEX,{"disambiguationData":[OD(0.0)],"derivedFrom":[subQ1,subQ0]});Q3=makeQuery(id+"F30.imprint","IMPRINT",FACE,{"disambiguationData":[TD([[makeQuery(id+"F30.imprint","IMPRINT",EDGE,{"disambiguationData":[TD([[subQ2,-1.0]])],"derivedFrom":subQ1}),1.0]])]});}
            var Q4;
            {var subQ0=sQuery(id+"F30.wireOp",EDGE,"E66.1");var subQ1=sQuery(id+"F30.wireOp",EDGE,"E65.bottom");var subQ2=makeQuery(id+"F30.imprint","INTERSECT",VERTEX,{"disambiguationData":[OD(0.0)],"derivedFrom":[subQ1,subQ0]});Q4=makeQuery(id+"F30.imprint","IMPRINT",FACE,{"disambiguationData":[TD([[makeQuery(id+"F30.imprint","IMPRINT",EDGE,{"disambiguationData":[TD([[subQ2,-1.0]])],"derivedFrom":subQ1}),-1.0]])]});}
            var Q5;
            {var subQ0=sQuery(id+"F30.wireOp",EDGE,"E66.1");var subQ1=sQuery(id+"F30.wireOp",EDGE,"E65.left");var subQ2=makeQuery(id+"F30.imprint","INTERSECT",VERTEX,{"disambiguationData":[OD(0.0)],"derivedFrom":[subQ1,subQ0]});Q5=makeQuery(id+"F30.imprint","IMPRINT",FACE,{"disambiguationData":[TD([[makeQuery(id+"F30.imprint","IMPRINT",EDGE,{"disambiguationData":[TD([[subQ2,-1.0]])],"derivedFrom":subQ1}),1.0]])]});}
            var Q6;
            {var subQ0=sQuery(id+"F30.wireOp",EDGE,"E66.1");var subQ1=sQuery(id+"F30.wireOp",EDGE,"E65.right");var subQ2=makeQuery(id+"F30.imprint","INTERSECT",VERTEX,{"disambiguationData":[OD(0.0)],"derivedFrom":[subQ1,subQ0]});Q6=makeQuery(id+"F30.imprint","IMPRINT",FACE,{"disambiguationData":[TD([[makeQuery(id+"F30.imprint","IMPRINT",EDGE,{"disambiguationData":[TD([[subQ2,-1.0]])],"derivedFrom":subQ1}),-1.0]])]});}
            var Q7;
            {var subQ0=sQuery(id+"F30.wireOp",EDGE,"E66.1");var subQ1=sQuery(id+"F30.wireOp",EDGE,"E65.top");var subQ2=makeQuery(id+"F30.imprint","INTERSECT",VERTEX,{"disambiguationData":[OD(0.0)],"derivedFrom":[subQ1,subQ0]});Q7=makeQuery(id+"F30.imprint","IMPRINT",FACE,{"disambiguationData":[TD([[makeQuery(id+"F30.imprint","IMPRINT",EDGE,{"disambiguationData":[TD([[subQ2,-1.0]])],"derivedFrom":subQ1}),1.0]])]});}
            extrude(context, id + "F31", {"entities" : qUnion([Q0, Q1, Q2, Q3, Q4, Q5, Q6, Q7]), "operationType" : NewBodyOperationType.ADD, "depth" : 3.86 * mm, "offsetDistance" : 25.4 * mm});
        }
        {
            var Q0;
            Q0=makeQuery(id+"F27.boolean.opBoolean","COPY",FACE,{"derivedFrom":makeQuery(id+"F27.opExtrude","CAP_FACE",FACE,{"disambiguationData":[OSD([sQuery(id+"F26.wireOp",EDGE,"E59.0")])],"isStart":false})});
            var sketch = newSketch(context, id + "F32", { "sketchPlane" : qUnion([Q0])});
            skLineSegment(sketch, "E67.0.0", {"start": v(-1.17, 9.14) * mm, "end": v(-3.48, 9.14) * mm});
            skArc(sketch, "E67.0.1", {"start": v(-3.48, 9.14) * mm, "mid": v(-2.33, 9.42) * mm, "end": v(-1.17, 9.14) * mm});
            skLineSegment(sketch, "E67.1.0", {"start": v(-4.58, 8.05) * mm, "end": v(-4.58, 5.74) * mm});
            skArc(sketch, "E67.1.1", {"start": v(-4.58, 5.74) * mm, "mid": v(-4.86, 6.9) * mm, "end": v(-4.58, 8.05) * mm});
            skLineSegment(sketch, "E67.2.0", {"start": v(-3.48, 4.65) * mm, "end": v(-1.17, 4.65) * mm});
            skArc(sketch, "E67.2.1", {"start": v(-1.17, 4.65) * mm, "mid": v(-2.33, 4.37) * mm, "end": v(-3.48, 4.65) * mm});
            skLineSegment(sketch, "E67.3.0", {"start": v(-0.08, 5.74) * mm, "end": v(-0.08, 8.05) * mm});
            skArc(sketch, "E67.3.1", {"start": v(-0.08, 8.05) * mm, "mid": v(0.2, 6.9) * mm, "end": v(-0.08, 5.74) * mm});
            skLineSegment(sketch, "E67.4.0", {"start": v(12.7, 9.14) * mm, "end": v(10.4, 9.14) * mm});
            skArc(sketch, "E67.4.1", {"start": v(10.4, 9.14) * mm, "mid": v(11.55, 9.42) * mm, "end": v(12.7, 9.14) * mm});
            skArc(sketch, "E67.5.0", {"start": v(9.3, 5.74) * mm, "mid": v(9.03, 6.9) * mm, "end": v(9.3, 8.05) * mm});
            skLineSegment(sketch, "E67.5.1", {"start": v(9.3, 8.05) * mm, "end": v(9.3, 5.74) * mm});
            skArc(sketch, "E67.6.0", {"start": v(12.7, 4.65) * mm, "mid": v(11.55, 4.37) * mm, "end": v(10.4, 4.65) * mm});
            skLineSegment(sketch, "E67.6.1", {"start": v(10.4, 4.65) * mm, "end": v(12.7, 4.65) * mm});
            skLineSegment(sketch, "E67.7.0", {"start": v(13.8, 5.74) * mm, "end": v(13.8, 8.05) * mm});
            skArc(sketch, "E67.7.1", {"start": v(13.8, 8.05) * mm, "mid": v(14.08, 6.9) * mm, "end": v(13.8, 5.74) * mm});
            skSolve(sketch);
        }
        {
            var Q0;
            Q0 = qSketchRegion(id + "F32", true);
            extrude(context, id + "F33", {"entities" : qUnion([Q0]), "operationType" : NewBodyOperationType.ADD, "depth" : 3.86 * mm, "offsetDistance" : 25.4 * mm});
        }
        {
            var Q0;
            Q0=makeQuery(id+"F9.boolean.opBoolean","MERGE",FACE,{"derivedFrom":[makeQuery(id+"F1.opExtrude","CAP_FACE",FACE,{"disambiguationData":[OSD([sQuery(id+"F0.wireOp",EDGE,"E0.bottom"),sQuery(id+"F0.wireOp",EDGE,"E0.top"),sQuery(id+"F0.wireOp",EDGE,"E0.left"),sQuery(id+"F0.wireOp",EDGE,"E0.right")])],"isStart":false}),makeQuery(id+"F9.opExtrude","CAP_FACE",FACE,{"disambiguationData":[OSD([sQuery(id+"F8.wireOp",EDGE,"E8")])],"isStart":false})]});
            var sketch = newSketch(context, id + "F34", { "sketchPlane" : qUnion([Q0])});
            skLineSegment(sketch, "E68", {"start": v(-12.61, -18.5) * mm, "end": v(15.28, 9.27) * mm, "construction": true});
            skLineSegment(sketch, "E69", {"start": v(-5.58, -14.76) * mm, "end": v(-8.75, -11.58) * mm});
            skLineSegment(sketch, "E70", {"start": v(-8.75, -11.58) * mm, "end": v(-5.57, -8.4) * mm});
            skLineSegment(sketch, "E71", {"start": v(-5.57, -8.4) * mm, "end": v(-2.4, -11.6) * mm});
            skLineSegment(sketch, "E72", {"start": v(-2.4, -11.6) * mm, "end": v(-5.58, -14.76) * mm});
            skLineSegment(sketch, "E73", {"start": v(-7.16, -10) * mm, "end": v(-3.99, -13.18) * mm});
            skPoint(sketch, "E74", {"position": v(-5.57, -11.58) * mm});
            skLineSegment(sketch, "E75.1.0", {"start": v(11.49, -11.53) * mm, "end": v(8.3, -14.7) * mm});
            skLineSegment(sketch, "E75.1.1", {"start": v(8.31, -8.34) * mm, "end": v(11.49, -11.53) * mm});
            skLineSegment(sketch, "E75.1.2", {"start": v(5.13, -11.51) * mm, "end": v(8.31, -8.34) * mm});
            skLineSegment(sketch, "E75.1.3", {"start": v(8.3, -14.7) * mm, "end": v(5.13, -11.51) * mm});
            skLineSegment(sketch, "E75.2.0", {"start": v(8.25, 5.54) * mm, "end": v(11.42, 2.35) * mm});
            skLineSegment(sketch, "E75.2.1", {"start": v(5.06, 2.37) * mm, "end": v(8.25, 5.54) * mm});
            skLineSegment(sketch, "E75.2.2", {"start": v(8.24, -0.82) * mm, "end": v(5.06, 2.37) * mm});
            skLineSegment(sketch, "E75.2.3", {"start": v(11.42, 2.35) * mm, "end": v(8.24, -0.82) * mm});
            skLineSegment(sketch, "E75.3.0", {"start": v(-8.82, 2.3) * mm, "end": v(-5.63, 5.48) * mm});
            skLineSegment(sketch, "E75.3.1", {"start": v(-5.65, -0.88) * mm, "end": v(-8.82, 2.3) * mm});
            skLineSegment(sketch, "E75.3.2", {"start": v(-2.46, 2.29) * mm, "end": v(-5.65, -0.88) * mm});
            skLineSegment(sketch, "E75.3.3", {"start": v(-5.63, 5.48) * mm, "end": v(-2.46, 2.29) * mm});
            skPoint(sketch, "E75.center", {"position": v(1.33, -4.61) * mm});
            skCircle(sketch, "E76.0", {"center": v(-5.57, -11.58) * mm, "radius": 2.53 * mm});
            skCircle(sketch, "E77.1.0", {"center": v(8.3, -11.52) * mm, "radius": 2.53 * mm});
            skCircle(sketch, "E77.2.0", {"center": v(8.24, 2.36) * mm, "radius": 2.53 * mm});
            skCircle(sketch, "E77.3.0", {"center": v(-5.64, 2.3) * mm, "radius": 2.53 * mm});
            skSolve(sketch);
        }
        {
            var Q0;
            {var subQ0=sQuery(id+"F34.wireOp",EDGE,"E77.1.0");var subQ1=sQuery(id+"F34.wireOp",EDGE,"E75.1.0");var subQ2=makeQuery(id+"F34.imprint","INTERSECT",VERTEX,{"disambiguationData":[OD(0.0)],"derivedFrom":[subQ1,subQ0]});Q0=makeQuery(id+"F34.imprint","IMPRINT",FACE,{"disambiguationData":[TD([[makeQuery(id+"F34.imprint","IMPRINT",EDGE,{"disambiguationData":[TD([[subQ2,-1.0]])],"derivedFrom":subQ1}),1.0]])]});}
            var Q1;
            {var subQ0=sQuery(id+"F34.wireOp",EDGE,"E77.1.0");var subQ1=sQuery(id+"F34.wireOp",EDGE,"E75.1.3");var subQ2=makeQuery(id+"F34.imprint","INTERSECT",VERTEX,{"disambiguationData":[OD(0.0)],"derivedFrom":[subQ1,subQ0]});Q1=makeQuery(id+"F34.imprint","IMPRINT",FACE,{"disambiguationData":[TD([[makeQuery(id+"F34.imprint","IMPRINT",EDGE,{"disambiguationData":[TD([[subQ2,-1.0]])],"derivedFrom":subQ1}),1.0]])]});}
            var Q2;
            {var subQ0=sQuery(id+"F34.wireOp",EDGE,"E77.1.0");var subQ1=sQuery(id+"F34.wireOp",EDGE,"E75.1.1");var subQ2=makeQuery(id+"F34.imprint","INTERSECT",VERTEX,{"disambiguationData":[OD(0.0)],"derivedFrom":[subQ1,subQ0]});Q2=makeQuery(id+"F34.imprint","IMPRINT",FACE,{"disambiguationData":[TD([[makeQuery(id+"F34.imprint","IMPRINT",EDGE,{"disambiguationData":[TD([[subQ2,-1.0]])],"derivedFrom":subQ1}),1.0]])]});}
            var Q3;
            {var subQ0=sQuery(id+"F34.wireOp",EDGE,"E77.1.0");var subQ1=sQuery(id+"F34.wireOp",EDGE,"E75.1.2");var subQ2=makeQuery(id+"F34.imprint","INTERSECT",VERTEX,{"disambiguationData":[OD(0.0)],"derivedFrom":[subQ1,subQ0]});Q3=makeQuery(id+"F34.imprint","IMPRINT",FACE,{"disambiguationData":[TD([[makeQuery(id+"F34.imprint","IMPRINT",EDGE,{"disambiguationData":[TD([[subQ2,-1.0]])],"derivedFrom":subQ1}),1.0]])]});}
            var Q4;
            {var subQ0=sQuery(id+"F34.wireOp",EDGE,"E70");var subQ1=makeQuery(id+"F34.imprint","INTERSECT",VERTEX,{"derivedFrom":[subQ0,sQuery(id+"F34.wireOp",EDGE,"E73")]});Q4=makeQuery(id+"F34.imprint","IMPRINT",FACE,{"disambiguationData":[TD([[makeQuery(id+"F34.imprint","IMPRINT",EDGE,{"disambiguationData":[TD([[subQ1,1.0]])],"derivedFrom":subQ0}),1.0]])]});}
            var Q5;
            {var subQ0=sQuery(id+"F34.wireOp",EDGE,"E76.0");var subQ1=sQuery(id+"F34.wireOp",EDGE,"E71");var subQ2=makeQuery(id+"F34.imprint","INTERSECT",VERTEX,{"disambiguationData":[OD(0.0)],"derivedFrom":[subQ1,subQ0]});Q5=makeQuery(id+"F34.imprint","IMPRINT",FACE,{"disambiguationData":[TD([[makeQuery(id+"F34.imprint","IMPRINT",EDGE,{"disambiguationData":[TD([[subQ2,-1.0]])],"derivedFrom":subQ1}),1.0]])]});}
            var Q6;
            {var subQ0=sQuery(id+"F34.wireOp",EDGE,"E72");var subQ1=makeQuery(id+"F34.imprint","INTERSECT",VERTEX,{"derivedFrom":[subQ0,sQuery(id+"F34.wireOp",EDGE,"E73")]});Q6=makeQuery(id+"F34.imprint","IMPRINT",FACE,{"disambiguationData":[TD([[makeQuery(id+"F34.imprint","IMPRINT",EDGE,{"disambiguationData":[TD([[subQ1,1.0]])],"derivedFrom":subQ0}),1.0]])]});}
            var Q7;
            {var subQ0=sQuery(id+"F34.wireOp",EDGE,"E76.0");var subQ1=sQuery(id+"F34.wireOp",EDGE,"E69");var subQ2=makeQuery(id+"F34.imprint","INTERSECT",VERTEX,{"disambiguationData":[OD(0.0)],"derivedFrom":[subQ1,subQ0]});Q7=makeQuery(id+"F34.imprint","IMPRINT",FACE,{"disambiguationData":[TD([[makeQuery(id+"F34.imprint","IMPRINT",EDGE,{"disambiguationData":[TD([[subQ2,-1.0]])],"derivedFrom":subQ1}),1.0]])]});}
            var Q8;
            {var subQ0=sQuery(id+"F34.wireOp",EDGE,"E77.3.0");var subQ1=sQuery(id+"F34.wireOp",EDGE,"E75.3.0");var subQ2=makeQuery(id+"F34.imprint","INTERSECT",VERTEX,{"disambiguationData":[OD(0.0)],"derivedFrom":[subQ1,subQ0]});Q8=makeQuery(id+"F34.imprint","IMPRINT",FACE,{"disambiguationData":[TD([[makeQuery(id+"F34.imprint","IMPRINT",EDGE,{"disambiguationData":[TD([[subQ2,-1.0]])],"derivedFrom":subQ1}),1.0]])]});}
            var Q9;
            {var subQ0=sQuery(id+"F34.wireOp",EDGE,"E77.3.0");var subQ1=sQuery(id+"F34.wireOp",EDGE,"E75.3.3");var subQ2=makeQuery(id+"F34.imprint","INTERSECT",VERTEX,{"disambiguationData":[OD(0.0)],"derivedFrom":[subQ1,subQ0]});Q9=makeQuery(id+"F34.imprint","IMPRINT",FACE,{"disambiguationData":[TD([[makeQuery(id+"F34.imprint","IMPRINT",EDGE,{"disambiguationData":[TD([[subQ2,-1.0]])],"derivedFrom":subQ1}),1.0]])]});}
            var Q10;
            {var subQ0=sQuery(id+"F34.wireOp",EDGE,"E77.3.0");var subQ1=sQuery(id+"F34.wireOp",EDGE,"E75.3.1");var subQ2=makeQuery(id+"F34.imprint","INTERSECT",VERTEX,{"disambiguationData":[OD(0.0)],"derivedFrom":[subQ1,subQ0]});Q10=makeQuery(id+"F34.imprint","IMPRINT",FACE,{"disambiguationData":[TD([[makeQuery(id+"F34.imprint","IMPRINT",EDGE,{"disambiguationData":[TD([[subQ2,-1.0]])],"derivedFrom":subQ1}),1.0]])]});}
            var Q11;
            {var subQ0=sQuery(id+"F34.wireOp",EDGE,"E77.3.0");var subQ1=sQuery(id+"F34.wireOp",EDGE,"E75.3.2");var subQ2=makeQuery(id+"F34.imprint","INTERSECT",VERTEX,{"disambiguationData":[OD(0.0)],"derivedFrom":[subQ1,subQ0]});Q11=makeQuery(id+"F34.imprint","IMPRINT",FACE,{"disambiguationData":[TD([[makeQuery(id+"F34.imprint","IMPRINT",EDGE,{"disambiguationData":[TD([[subQ2,-1.0]])],"derivedFrom":subQ1}),1.0]])]});}
            var Q12;
            {var subQ0=sQuery(id+"F34.wireOp",EDGE,"E77.2.0");var subQ1=sQuery(id+"F34.wireOp",EDGE,"E75.2.0");var subQ2=makeQuery(id+"F34.imprint","INTERSECT",VERTEX,{"disambiguationData":[OD(0.0)],"derivedFrom":[subQ1,subQ0]});Q12=makeQuery(id+"F34.imprint","IMPRINT",FACE,{"disambiguationData":[TD([[makeQuery(id+"F34.imprint","IMPRINT",EDGE,{"disambiguationData":[TD([[subQ2,-1.0]])],"derivedFrom":subQ1}),1.0]])]});}
            var Q13;
            {var subQ0=sQuery(id+"F34.wireOp",EDGE,"E77.2.0");var subQ1=sQuery(id+"F34.wireOp",EDGE,"E75.2.1");var subQ2=makeQuery(id+"F34.imprint","INTERSECT",VERTEX,{"disambiguationData":[OD(0.0)],"derivedFrom":[subQ1,subQ0]});Q13=makeQuery(id+"F34.imprint","IMPRINT",FACE,{"disambiguationData":[TD([[makeQuery(id+"F34.imprint","IMPRINT",EDGE,{"disambiguationData":[TD([[subQ2,-1.0]])],"derivedFrom":subQ1}),1.0]])]});}
            var Q14;
            {var subQ0=sQuery(id+"F34.wireOp",EDGE,"E77.2.0");var subQ1=sQuery(id+"F34.wireOp",EDGE,"E75.2.2");var subQ2=makeQuery(id+"F34.imprint","INTERSECT",VERTEX,{"disambiguationData":[OD(0.0)],"derivedFrom":[subQ1,subQ0]});Q14=makeQuery(id+"F34.imprint","IMPRINT",FACE,{"disambiguationData":[TD([[makeQuery(id+"F34.imprint","IMPRINT",EDGE,{"disambiguationData":[TD([[subQ2,-1.0]])],"derivedFrom":subQ1}),1.0]])]});}
            var Q15;
            {var subQ0=sQuery(id+"F34.wireOp",EDGE,"E77.2.0");var subQ1=sQuery(id+"F34.wireOp",EDGE,"E75.2.3");var subQ2=makeQuery(id+"F34.imprint","INTERSECT",VERTEX,{"disambiguationData":[OD(0.0)],"derivedFrom":[subQ1,subQ0]});Q15=makeQuery(id+"F34.imprint","IMPRINT",FACE,{"disambiguationData":[TD([[makeQuery(id+"F34.imprint","IMPRINT",EDGE,{"disambiguationData":[TD([[subQ2,-1.0]])],"derivedFrom":subQ1}),1.0]])]});}
            extrude(context, id + "F35", {"entities" : qUnion([Q0, Q1, Q2, Q3, Q4, Q5, Q6, Q7, Q8, Q9, Q10, Q11, Q12, Q13, Q14, Q15]), "operationType" : NewBodyOperationType.ADD, "oppositeDirection" : true, "depth" : 13.8 * mm, "offsetDistance" : 25.4 * mm});
        }
        {
            var Q0;
            {var subQ0=sQuery(id+"F34.wireOp",EDGE,"E77.3.0");var subQ1=sQuery(id+"F34.wireOp",EDGE,"E77.2.0");var subQ2=sQuery(id+"F34.wireOp",EDGE,"E77.1.0");var subQ3=sQuery(id+"F34.wireOp",EDGE,"E76.0");Q0=makeQuery(id+"F35.boolean.opBoolean","MERGE",FACE,{"derivedFrom":[makeQuery(id+"F9.boolean.opBoolean","MERGE",FACE,{"derivedFrom":[makeQuery(id+"F1.opExtrude","CAP_FACE",FACE,{"disambiguationData":[OSD([sQuery(id+"F0.wireOp",EDGE,"E0.bottom"),sQuery(id+"F0.wireOp",EDGE,"E0.top"),sQuery(id+"F0.wireOp",EDGE,"E0.left"),sQuery(id+"F0.wireOp",EDGE,"E0.right")])],"isStart":false}),makeQuery(id+"F9.opExtrude","CAP_FACE",FACE,{"disambiguationData":[OSD([sQuery(id+"F8.wireOp",EDGE,"E8")])],"isStart":false})]}),makeQuery(id+"F35.opExtrude","CAP_FACE",FACE,{"disambiguationData":[OSD([sQuery(id+"F34.wireOp",EDGE,"E69"),subQ3])],"isStart":true}),makeQuery(id+"F35.opExtrude","CAP_FACE",FACE,{"disambiguationData":[OSD([sQuery(id+"F34.wireOp",EDGE,"E70"),subQ3])],"isStart":true}),makeQuery(id+"F35.opExtrude","CAP_FACE",FACE,{"disambiguationData":[OSD([sQuery(id+"F34.wireOp",EDGE,"E71"),subQ3])],"isStart":true}),makeQuery(id+"F35.opExtrude","CAP_FACE",FACE,{"disambiguationData":[OSD([sQuery(id+"F34.wireOp",EDGE,"E72"),subQ3])],"isStart":true}),makeQuery(id+"F35.opExtrude","CAP_FACE",FACE,{"disambiguationData":[OSD([sQuery(id+"F34.wireOp",EDGE,"E75.1.0"),subQ2])],"isStart":true}),makeQuery(id+"F35.opExtrude","CAP_FACE",FACE,{"disambiguationData":[OSD([sQuery(id+"F34.wireOp",EDGE,"E75.1.1"),subQ2])],"isStart":true}),makeQuery(id+"F35.opExtrude","CAP_FACE",FACE,{"disambiguationData":[OSD([sQuery(id+"F34.wireOp",EDGE,"E75.1.2"),subQ2])],"isStart":true}),makeQuery(id+"F35.opExtrude","CAP_FACE",FACE,{"disambiguationData":[OSD([sQuery(id+"F34.wireOp",EDGE,"E75.1.3"),subQ2])],"isStart":true}),makeQuery(id+"F35.opExtrude","CAP_FACE",FACE,{"disambiguationData":[OSD([sQuery(id+"F34.wireOp",EDGE,"E75.2.0"),subQ1])],"isStart":true}),makeQuery(id+"F35.opExtrude","CAP_FACE",FACE,{"disambiguationData":[OSD([sQuery(id+"F34.wireOp",EDGE,"E75.2.1"),subQ1])],"isStart":true}),makeQuery(id+"F35.opExtrude","CAP_FACE",FACE,{"disambiguationData":[OSD([sQuery(id+"F34.wireOp",EDGE,"E75.2.2"),subQ1])],"isStart":true}),makeQuery(id+"F35.opExtrude","CAP_FACE",FACE,{"disambiguationData":[OSD([sQuery(id+"F34.wireOp",EDGE,"E75.2.3"),subQ1])],"isStart":true}),makeQuery(id+"F35.opExtrude","CAP_FACE",FACE,{"disambiguationData":[OSD([sQuery(id+"F34.wireOp",EDGE,"E75.3.0"),subQ0])],"isStart":true}),makeQuery(id+"F35.opExtrude","CAP_FACE",FACE,{"disambiguationData":[OSD([sQuery(id+"F34.wireOp",EDGE,"E75.3.1"),subQ0])],"isStart":true}),makeQuery(id+"F35.opExtrude","CAP_FACE",FACE,{"disambiguationData":[OSD([sQuery(id+"F34.wireOp",EDGE,"E75.3.2"),subQ0])],"isStart":true}),makeQuery(id+"F35.opExtrude","CAP_FACE",FACE,{"disambiguationData":[OSD([sQuery(id+"F34.wireOp",EDGE,"E75.3.3"),subQ0])],"isStart":true})]});}
            var sketch = newSketch(context, id + "F36", { "sketchPlane" : qUnion([Q0])});
            skCircle(sketch, "E78", {"center": v(8.24, 2.36) * mm, "radius": 2.53 * mm});
            skLineSegment(sketch, "E79.0", {"start": v(10.65, 1.58) * mm, "end": v(9.01, -0.05) * mm});
            skLineSegment(sketch, "E79.1", {"start": v(9.02, 4.76) * mm, "end": v(10.65, 3.13) * mm});
            skLineSegment(sketch, "E79.2", {"start": v(5.84, 3.14) * mm, "end": v(7.48, 4.77) * mm});
            skLineSegment(sketch, "E79.3", {"start": v(7.46, -0.04) * mm, "end": v(5.84, 1.6) * mm});
            skCircle(sketch, "E80.1.0", {"center": v(-5.64, 2.3) * mm, "radius": 2.53 * mm});
            skLineSegment(sketch, "E80.1.1", {"start": v(-4.86, 4.7) * mm, "end": v(-3.23, 3.06) * mm});
            skLineSegment(sketch, "E80.1.2", {"start": v(-8.04, 3.07) * mm, "end": v(-6.4, 4.7) * mm});
            skLineSegment(sketch, "E80.1.3", {"start": v(-6.42, -0.1) * mm, "end": v(-8.05, 1.53) * mm});
            skLineSegment(sketch, "E80.1.4", {"start": v(-3.23, 1.52) * mm, "end": v(-4.87, -0.11) * mm});
            skCircle(sketch, "E80.2.0", {"center": v(-5.57, -11.58) * mm, "radius": 2.53 * mm});
            skLineSegment(sketch, "E80.2.1", {"start": v(-7.98, -10.8) * mm, "end": v(-6.34, -9.18) * mm});
            skLineSegment(sketch, "E80.2.2", {"start": v(-6.35, -13.99) * mm, "end": v(-7.98, -12.35) * mm});
            skLineSegment(sketch, "E80.2.3", {"start": v(-3.17, -12.36) * mm, "end": v(-4.8, -14) * mm});
            skLineSegment(sketch, "E80.2.4", {"start": v(-4.8, -9.18) * mm, "end": v(-3.17, -10.82) * mm});
            skCircle(sketch, "E80.3.0", {"center": v(8.3, -11.52) * mm, "radius": 2.53 * mm});
            skLineSegment(sketch, "E80.3.1", {"start": v(7.53, -13.93) * mm, "end": v(5.9, -12.29) * mm});
            skLineSegment(sketch, "E80.3.2", {"start": v(10.71, -12.3) * mm, "end": v(9.07, -13.93) * mm});
            skLineSegment(sketch, "E80.3.3", {"start": v(9.08, -9.12) * mm, "end": v(10.71, -10.75) * mm});
            skLineSegment(sketch, "E80.3.4", {"start": v(5.9, -10.74) * mm, "end": v(7.54, -9.11) * mm});
            skPoint(sketch, "E80.center", {"position": v(1.33, -4.61) * mm});
            skSolve(sketch);
        }
        {
            var Q0;
            {var subQ0=sQuery(id+"F36.wireOp",EDGE,"E79.1");var subQ1=sQuery(id+"F36.wireOp",EDGE,"E78");var subQ2=makeQuery(id+"F36.imprint","INTERSECT",VERTEX,{"disambiguationData":[OD(0.0)],"derivedFrom":[subQ1,subQ0]});Q0=makeQuery(id+"F36.imprint","IMPRINT",FACE,{"disambiguationData":[TD([[makeQuery(id+"F36.imprint","IMPRINT",EDGE,{"disambiguationData":[TD([[subQ2,1.0]])],"derivedFrom":subQ1}),1.0]])]});}
            var Q1;
            {var subQ0=sQuery(id+"F36.wireOp",EDGE,"E79.2");var subQ1=sQuery(id+"F36.wireOp",EDGE,"E78");var subQ2=makeQuery(id+"F36.imprint","INTERSECT",VERTEX,{"disambiguationData":[OD(0.0)],"derivedFrom":[subQ1,subQ0]});Q1=makeQuery(id+"F36.imprint","IMPRINT",FACE,{"disambiguationData":[TD([[makeQuery(id+"F36.imprint","IMPRINT",EDGE,{"disambiguationData":[TD([[subQ2,-1.0]])],"derivedFrom":subQ1}),1.0]])]});}
            var Q2;
            {var subQ0=sQuery(id+"F36.wireOp",EDGE,"E79.3");var subQ1=sQuery(id+"F36.wireOp",EDGE,"E78");var subQ2=makeQuery(id+"F36.imprint","INTERSECT",VERTEX,{"disambiguationData":[OD(0.0)],"derivedFrom":[subQ1,subQ0]});Q2=makeQuery(id+"F36.imprint","IMPRINT",FACE,{"disambiguationData":[TD([[makeQuery(id+"F36.imprint","IMPRINT",EDGE,{"disambiguationData":[TD([[subQ2,-1.0]])],"derivedFrom":subQ1}),1.0]])]});}
            var Q3;
            {var subQ0=sQuery(id+"F36.wireOp",EDGE,"E79.0");var subQ1=sQuery(id+"F36.wireOp",EDGE,"E78");var subQ2=makeQuery(id+"F36.imprint","INTERSECT",VERTEX,{"disambiguationData":[OD(0.0)],"derivedFrom":[subQ1,subQ0]});Q3=makeQuery(id+"F36.imprint","IMPRINT",FACE,{"disambiguationData":[TD([[makeQuery(id+"F36.imprint","IMPRINT",EDGE,{"disambiguationData":[TD([[subQ2,-1.0]])],"derivedFrom":subQ1}),1.0]])]});}
            var Q4;
            {var subQ0=sQuery(id+"F36.wireOp",EDGE,"E80.1.2");var subQ1=sQuery(id+"F36.wireOp",EDGE,"E80.1.0");var subQ2=makeQuery(id+"F36.imprint","INTERSECT",VERTEX,{"disambiguationData":[OD(0.0)],"derivedFrom":[subQ1,subQ0]});Q4=makeQuery(id+"F36.imprint","IMPRINT",FACE,{"disambiguationData":[TD([[makeQuery(id+"F36.imprint","IMPRINT",EDGE,{"disambiguationData":[TD([[subQ2,1.0]])],"derivedFrom":subQ1}),1.0]])]});}
            var Q5;
            {var subQ0=sQuery(id+"F36.wireOp",EDGE,"E80.1.3");var subQ1=sQuery(id+"F36.wireOp",EDGE,"E80.1.0");var subQ2=makeQuery(id+"F36.imprint","INTERSECT",VERTEX,{"disambiguationData":[OD(0.0)],"derivedFrom":[subQ1,subQ0]});Q5=makeQuery(id+"F36.imprint","IMPRINT",FACE,{"disambiguationData":[TD([[makeQuery(id+"F36.imprint","IMPRINT",EDGE,{"disambiguationData":[TD([[subQ2,-1.0]])],"derivedFrom":subQ1}),1.0]])]});}
            var Q6;
            {var subQ0=sQuery(id+"F36.wireOp",EDGE,"E80.1.4");var subQ1=sQuery(id+"F36.wireOp",EDGE,"E80.1.0");var subQ2=makeQuery(id+"F36.imprint","INTERSECT",VERTEX,{"disambiguationData":[OD(0.0)],"derivedFrom":[subQ1,subQ0]});Q6=makeQuery(id+"F36.imprint","IMPRINT",FACE,{"disambiguationData":[TD([[makeQuery(id+"F36.imprint","IMPRINT",EDGE,{"disambiguationData":[TD([[subQ2,-1.0]])],"derivedFrom":subQ1}),1.0]])]});}
            var Q7;
            {var subQ0=sQuery(id+"F36.wireOp",EDGE,"E80.1.1");var subQ1=sQuery(id+"F36.wireOp",EDGE,"E80.1.0");var subQ2=makeQuery(id+"F36.imprint","INTERSECT",VERTEX,{"disambiguationData":[OD(0.0)],"derivedFrom":[subQ1,subQ0]});Q7=makeQuery(id+"F36.imprint","IMPRINT",FACE,{"disambiguationData":[TD([[makeQuery(id+"F36.imprint","IMPRINT",EDGE,{"disambiguationData":[TD([[subQ2,-1.0]])],"derivedFrom":subQ1}),1.0]])]});}
            var Q8;
            {var subQ0=sQuery(id+"F36.wireOp",EDGE,"E80.2.2");var subQ1=sQuery(id+"F36.wireOp",EDGE,"E80.2.0");var subQ2=makeQuery(id+"F36.imprint","INTERSECT",VERTEX,{"disambiguationData":[OD(0.0)],"derivedFrom":[subQ1,subQ0]});Q8=makeQuery(id+"F36.imprint","IMPRINT",FACE,{"disambiguationData":[TD([[makeQuery(id+"F36.imprint","IMPRINT",EDGE,{"disambiguationData":[TD([[subQ2,1.0]])],"derivedFrom":subQ1}),1.0]])]});}
            var Q9;
            {var subQ0=sQuery(id+"F36.wireOp",EDGE,"E80.2.3");var subQ1=sQuery(id+"F36.wireOp",EDGE,"E80.2.0");var subQ2=makeQuery(id+"F36.imprint","INTERSECT",VERTEX,{"disambiguationData":[OD(0.0)],"derivedFrom":[subQ1,subQ0]});Q9=makeQuery(id+"F36.imprint","IMPRINT",FACE,{"disambiguationData":[TD([[makeQuery(id+"F36.imprint","IMPRINT",EDGE,{"disambiguationData":[TD([[subQ2,-1.0]])],"derivedFrom":subQ1}),1.0]])]});}
            var Q10;
            {var subQ0=sQuery(id+"F36.wireOp",EDGE,"E80.2.4");var subQ1=sQuery(id+"F36.wireOp",EDGE,"E80.2.0");var subQ2=makeQuery(id+"F36.imprint","INTERSECT",VERTEX,{"disambiguationData":[OD(0.0)],"derivedFrom":[subQ1,subQ0]});Q10=makeQuery(id+"F36.imprint","IMPRINT",FACE,{"disambiguationData":[TD([[makeQuery(id+"F36.imprint","IMPRINT",EDGE,{"disambiguationData":[TD([[subQ2,-1.0]])],"derivedFrom":subQ1}),1.0]])]});}
            var Q11;
            {var subQ0=sQuery(id+"F36.wireOp",EDGE,"E80.2.1");var subQ1=sQuery(id+"F36.wireOp",EDGE,"E80.2.0");var subQ2=makeQuery(id+"F36.imprint","INTERSECT",VERTEX,{"disambiguationData":[OD(0.0)],"derivedFrom":[subQ1,subQ0]});Q11=makeQuery(id+"F36.imprint","IMPRINT",FACE,{"disambiguationData":[TD([[makeQuery(id+"F36.imprint","IMPRINT",EDGE,{"disambiguationData":[TD([[subQ2,-1.0]])],"derivedFrom":subQ1}),1.0]])]});}
            var Q12;
            {var subQ0=sQuery(id+"F36.wireOp",EDGE,"E80.3.2");var subQ1=sQuery(id+"F36.wireOp",EDGE,"E80.3.0");var subQ2=makeQuery(id+"F36.imprint","INTERSECT",VERTEX,{"disambiguationData":[OD(0.0)],"derivedFrom":[subQ1,subQ0]});Q12=makeQuery(id+"F36.imprint","IMPRINT",FACE,{"disambiguationData":[TD([[makeQuery(id+"F36.imprint","IMPRINT",EDGE,{"disambiguationData":[TD([[subQ2,1.0]])],"derivedFrom":subQ1}),1.0]])]});}
            var Q13;
            {var subQ0=sQuery(id+"F36.wireOp",EDGE,"E80.3.3");var subQ1=sQuery(id+"F36.wireOp",EDGE,"E80.3.0");var subQ2=makeQuery(id+"F36.imprint","INTERSECT",VERTEX,{"disambiguationData":[OD(0.0)],"derivedFrom":[subQ1,subQ0]});Q13=makeQuery(id+"F36.imprint","IMPRINT",FACE,{"disambiguationData":[TD([[makeQuery(id+"F36.imprint","IMPRINT",EDGE,{"disambiguationData":[TD([[subQ2,-1.0]])],"derivedFrom":subQ1}),1.0]])]});}
            var Q14;
            {var subQ0=sQuery(id+"F36.wireOp",EDGE,"E80.3.4");var subQ1=sQuery(id+"F36.wireOp",EDGE,"E80.3.0");var subQ2=makeQuery(id+"F36.imprint","INTERSECT",VERTEX,{"disambiguationData":[OD(0.0)],"derivedFrom":[subQ1,subQ0]});Q14=makeQuery(id+"F36.imprint","IMPRINT",FACE,{"disambiguationData":[TD([[makeQuery(id+"F36.imprint","IMPRINT",EDGE,{"disambiguationData":[TD([[subQ2,-1.0]])],"derivedFrom":subQ1}),1.0]])]});}
            var Q15;
            {var subQ0=sQuery(id+"F36.wireOp",EDGE,"E80.3.1");var subQ1=sQuery(id+"F36.wireOp",EDGE,"E80.3.0");var subQ2=makeQuery(id+"F36.imprint","INTERSECT",VERTEX,{"disambiguationData":[OD(0.0)],"derivedFrom":[subQ1,subQ0]});Q15=makeQuery(id+"F36.imprint","IMPRINT",FACE,{"disambiguationData":[TD([[makeQuery(id+"F36.imprint","IMPRINT",EDGE,{"disambiguationData":[TD([[subQ2,-1.0]])],"derivedFrom":subQ1}),1.0]])]});}
            extrude(context, id + "F37", {"entities" : qUnion([Q0, Q1, Q2, Q3, Q4, Q5, Q6, Q7, Q8, Q9, Q10, Q11, Q12, Q13, Q14, Q15]), "operationType" : NewBodyOperationType.REMOVE, "oppositeDirection" : true, "depth" : 0.38 * mm, "offsetDistance" : 25.4 * mm});
        }
        {
            var Q0;
            {var subQ0=sQuery(id+"F34.wireOp",EDGE,"E77.3.0");var subQ1=sQuery(id+"F34.wireOp",EDGE,"E77.2.0");var subQ2=sQuery(id+"F34.wireOp",EDGE,"E77.1.0");var subQ3=sQuery(id+"F34.wireOp",EDGE,"E76.0");Q0=makeQuery(id+"F35.boolean.opBoolean","MERGE",FACE,{"derivedFrom":[makeQuery(id+"F7.boolean.opBoolean","MERGE",FACE,{"derivedFrom":[makeQuery(id+"F1.opExtrude","CAP_FACE",FACE,{"disambiguationData":[OSD([sQuery(id+"F0.wireOp",EDGE,"E0.bottom"),sQuery(id+"F0.wireOp",EDGE,"E0.top"),sQuery(id+"F0.wireOp",EDGE,"E0.left"),sQuery(id+"F0.wireOp",EDGE,"E0.right")])],"isStart":true}),makeQuery(id+"F7.opExtrude","CAP_FACE",FACE,{"disambiguationData":[OSD([sQuery(id+"F6.wireOp",EDGE,"E5")])],"isStart":false})]}),makeQuery(id+"F35.opExtrude","CAP_FACE",FACE,{"disambiguationData":[OSD([sQuery(id+"F34.wireOp",EDGE,"E69"),subQ3])],"isStart":false}),makeQuery(id+"F35.opExtrude","CAP_FACE",FACE,{"disambiguationData":[OSD([sQuery(id+"F34.wireOp",EDGE,"E70"),subQ3])],"isStart":false}),makeQuery(id+"F35.opExtrude","CAP_FACE",FACE,{"disambiguationData":[OSD([sQuery(id+"F34.wireOp",EDGE,"E71"),subQ3])],"isStart":false}),makeQuery(id+"F35.opExtrude","CAP_FACE",FACE,{"disambiguationData":[OSD([sQuery(id+"F34.wireOp",EDGE,"E72"),subQ3])],"isStart":false}),makeQuery(id+"F35.opExtrude","CAP_FACE",FACE,{"disambiguationData":[OSD([sQuery(id+"F34.wireOp",EDGE,"E75.1.0"),subQ2])],"isStart":false}),makeQuery(id+"F35.opExtrude","CAP_FACE",FACE,{"disambiguationData":[OSD([sQuery(id+"F34.wireOp",EDGE,"E75.1.1"),subQ2])],"isStart":false}),makeQuery(id+"F35.opExtrude","CAP_FACE",FACE,{"disambiguationData":[OSD([sQuery(id+"F34.wireOp",EDGE,"E75.1.2"),subQ2])],"isStart":false}),makeQuery(id+"F35.opExtrude","CAP_FACE",FACE,{"disambiguationData":[OSD([sQuery(id+"F34.wireOp",EDGE,"E75.1.3"),subQ2])],"isStart":false}),makeQuery(id+"F35.opExtrude","CAP_FACE",FACE,{"disambiguationData":[OSD([sQuery(id+"F34.wireOp",EDGE,"E75.2.0"),subQ1])],"isStart":false}),makeQuery(id+"F35.opExtrude","CAP_FACE",FACE,{"disambiguationData":[OSD([sQuery(id+"F34.wireOp",EDGE,"E75.2.1"),subQ1])],"isStart":false}),makeQuery(id+"F35.opExtrude","CAP_FACE",FACE,{"disambiguationData":[OSD([sQuery(id+"F34.wireOp",EDGE,"E75.2.2"),subQ1])],"isStart":false}),makeQuery(id+"F35.opExtrude","CAP_FACE",FACE,{"disambiguationData":[OSD([sQuery(id+"F34.wireOp",EDGE,"E75.2.3"),subQ1])],"isStart":false}),makeQuery(id+"F35.opExtrude","CAP_FACE",FACE,{"disambiguationData":[OSD([sQuery(id+"F34.wireOp",EDGE,"E75.3.0"),subQ0])],"isStart":false}),makeQuery(id+"F35.opExtrude","CAP_FACE",FACE,{"disambiguationData":[OSD([sQuery(id+"F34.wireOp",EDGE,"E75.3.1"),subQ0])],"isStart":false}),makeQuery(id+"F35.opExtrude","CAP_FACE",FACE,{"disambiguationData":[OSD([sQuery(id+"F34.wireOp",EDGE,"E75.3.2"),subQ0])],"isStart":false}),makeQuery(id+"F35.opExtrude","CAP_FACE",FACE,{"disambiguationData":[OSD([sQuery(id+"F34.wireOp",EDGE,"E75.3.3"),subQ0])],"isStart":false})]});}
            var sketch = newSketch(context, id + "F38", { "sketchPlane" : qUnion([Q0])});
            skCircle(sketch, "E81", {"center": v(8.24, -2.36) * mm, "radius": 2.53 * mm});
            skLineSegment(sketch, "E82.0", {"start": v(5.84, -3.14) * mm, "end": v(7.48, -4.77) * mm});
            skLineSegment(sketch, "E82.1", {"start": v(9.02, -4.76) * mm, "end": v(10.65, -3.13) * mm});
            skLineSegment(sketch, "E82.3", {"start": v(10.65, -1.58) * mm, "end": v(9.01, 0.05) * mm});
            skLineSegment(sketch, "E82.4", {"start": v(7.46, 0.04) * mm, "end": v(5.84, -1.6) * mm});
            skCircle(sketch, "E83.1.0", {"center": v(8.3, 11.52) * mm, "radius": 2.53 * mm});
            skLineSegment(sketch, "E83.1.1", {"start": v(5.9, 10.74) * mm, "end": v(7.54, 9.11) * mm});
            skLineSegment(sketch, "E83.1.2", {"start": v(9.08, 9.12) * mm, "end": v(10.71, 10.75) * mm});
            skLineSegment(sketch, "E83.1.3", {"start": v(10.71, 12.3) * mm, "end": v(9.07, 13.93) * mm});
            skLineSegment(sketch, "E83.1.4", {"start": v(7.53, 13.93) * mm, "end": v(5.9, 12.29) * mm});
            skCircle(sketch, "E83.2.0", {"center": v(-5.57, 11.58) * mm, "radius": 2.53 * mm});
            skLineSegment(sketch, "E83.2.1", {"start": v(-4.8, 9.18) * mm, "end": v(-3.17, 10.82) * mm});
            skLineSegment(sketch, "E83.2.2", {"start": v(-3.17, 12.36) * mm, "end": v(-4.8, 14) * mm});
            skLineSegment(sketch, "E83.2.3", {"start": v(-6.35, 13.99) * mm, "end": v(-7.98, 12.35) * mm});
            skLineSegment(sketch, "E83.2.4", {"start": v(-7.98, 10.8) * mm, "end": v(-6.34, 9.18) * mm});
            skCircle(sketch, "E83.3.0", {"center": v(-5.64, -2.3) * mm, "radius": 2.53 * mm});
            skLineSegment(sketch, "E83.3.1", {"start": v(-3.23, -1.52) * mm, "end": v(-4.87, 0.11) * mm});
            skLineSegment(sketch, "E83.3.2", {"start": v(-6.42, 0.1) * mm, "end": v(-8.05, -1.53) * mm});
            skLineSegment(sketch, "E83.3.3", {"start": v(-8.04, -3.07) * mm, "end": v(-6.4, -4.7) * mm});
            skLineSegment(sketch, "E83.3.4", {"start": v(-4.86, -4.7) * mm, "end": v(-3.23, -3.06) * mm});
            skPoint(sketch, "E83.center", {"position": v(1.33, 4.61) * mm});
            skSolve(sketch);
        }
        {
            var Q0;
            {var subQ0=sQuery(id+"F38.wireOp",EDGE,"E82.3");Q0=makeQuery(id+"F38.imprint","IMPRINT",FACE,{"disambiguationData":[TD([[makeQuery(id+"F38.imprint","IMPRINT",EDGE,{"derivedFrom":subQ0}),-1.0]])]});}
            var Q1;
            {var subQ0=sQuery(id+"F38.wireOp",EDGE,"E82.4");Q1=makeQuery(id+"F38.imprint","IMPRINT",FACE,{"disambiguationData":[TD([[makeQuery(id+"F38.imprint","IMPRINT",EDGE,{"derivedFrom":subQ0}),-1.0]])]});}
            var Q2;
            {var subQ0=sQuery(id+"F38.wireOp",EDGE,"E82.0");Q2=makeQuery(id+"F38.imprint","IMPRINT",FACE,{"disambiguationData":[TD([[makeQuery(id+"F38.imprint","IMPRINT",EDGE,{"derivedFrom":subQ0}),-1.0]])]});}
            var Q3;
            {var subQ0=sQuery(id+"F38.wireOp",EDGE,"E82.1");Q3=makeQuery(id+"F38.imprint","IMPRINT",FACE,{"disambiguationData":[TD([[makeQuery(id+"F38.imprint","IMPRINT",EDGE,{"derivedFrom":subQ0}),-1.0]])]});}
            var Q4;
            {var subQ0=sQuery(id+"F38.wireOp",EDGE,"E83.1.4");Q4=makeQuery(id+"F38.imprint","IMPRINT",FACE,{"disambiguationData":[TD([[makeQuery(id+"F38.imprint","IMPRINT",EDGE,{"derivedFrom":subQ0}),-1.0]])]});}
            var Q5;
            {var subQ0=sQuery(id+"F38.wireOp",EDGE,"E83.1.1");Q5=makeQuery(id+"F38.imprint","IMPRINT",FACE,{"disambiguationData":[TD([[makeQuery(id+"F38.imprint","IMPRINT",EDGE,{"derivedFrom":subQ0}),-1.0]])]});}
            var Q6;
            {var subQ0=sQuery(id+"F38.wireOp",EDGE,"E83.1.2");Q6=makeQuery(id+"F38.imprint","IMPRINT",FACE,{"disambiguationData":[TD([[makeQuery(id+"F38.imprint","IMPRINT",EDGE,{"derivedFrom":subQ0}),-1.0]])]});}
            var Q7;
            {var subQ0=sQuery(id+"F38.wireOp",EDGE,"E83.1.3");Q7=makeQuery(id+"F38.imprint","IMPRINT",FACE,{"disambiguationData":[TD([[makeQuery(id+"F38.imprint","IMPRINT",EDGE,{"derivedFrom":subQ0}),-1.0]])]});}
            var Q8;
            {var subQ0=sQuery(id+"F38.wireOp",EDGE,"E83.2.4");Q8=makeQuery(id+"F38.imprint","IMPRINT",FACE,{"disambiguationData":[TD([[makeQuery(id+"F38.imprint","IMPRINT",EDGE,{"derivedFrom":subQ0}),-1.0]])]});}
            var Q9;
            {var subQ0=sQuery(id+"F38.wireOp",EDGE,"E83.2.1");Q9=makeQuery(id+"F38.imprint","IMPRINT",FACE,{"disambiguationData":[TD([[makeQuery(id+"F38.imprint","IMPRINT",EDGE,{"derivedFrom":subQ0}),-1.0]])]});}
            var Q10;
            {var subQ0=sQuery(id+"F38.wireOp",EDGE,"E83.2.2");Q10=makeQuery(id+"F38.imprint","IMPRINT",FACE,{"disambiguationData":[TD([[makeQuery(id+"F38.imprint","IMPRINT",EDGE,{"derivedFrom":subQ0}),-1.0]])]});}
            var Q11;
            {var subQ0=sQuery(id+"F38.wireOp",EDGE,"E83.2.3");Q11=makeQuery(id+"F38.imprint","IMPRINT",FACE,{"disambiguationData":[TD([[makeQuery(id+"F38.imprint","IMPRINT",EDGE,{"derivedFrom":subQ0}),-1.0]])]});}
            var Q12;
            {var subQ0=sQuery(id+"F38.wireOp",EDGE,"E83.3.4");Q12=makeQuery(id+"F38.imprint","IMPRINT",FACE,{"disambiguationData":[TD([[makeQuery(id+"F38.imprint","IMPRINT",EDGE,{"derivedFrom":subQ0}),-1.0]])]});}
            var Q13;
            {var subQ0=sQuery(id+"F38.wireOp",EDGE,"E83.3.1");Q13=makeQuery(id+"F38.imprint","IMPRINT",FACE,{"disambiguationData":[TD([[makeQuery(id+"F38.imprint","IMPRINT",EDGE,{"derivedFrom":subQ0}),-1.0]])]});}
            var Q14;
            {var subQ0=sQuery(id+"F38.wireOp",EDGE,"E83.3.2");Q14=makeQuery(id+"F38.imprint","IMPRINT",FACE,{"disambiguationData":[TD([[makeQuery(id+"F38.imprint","IMPRINT",EDGE,{"derivedFrom":subQ0}),-1.0]])]});}
            var Q15;
            {var subQ0=sQuery(id+"F38.wireOp",EDGE,"E83.3.3");Q15=makeQuery(id+"F38.imprint","IMPRINT",FACE,{"disambiguationData":[TD([[makeQuery(id+"F38.imprint","IMPRINT",EDGE,{"derivedFrom":subQ0}),-1.0]])]});}
            extrude(context, id + "F39", {"entities" : qUnion([Q0, Q1, Q2, Q3, Q4, Q5, Q6, Q7, Q8, Q9, Q10, Q11, Q12, Q13, Q14, Q15]), "operationType" : NewBodyOperationType.REMOVE, "oppositeDirection" : true, "depth" : 0.38 * mm, "offsetDistance" : 25.4 * mm});
        }
        {
            var Q0;
            Q0=makeQuery(id+"F1.opExtrude","CAP_EDGE",EDGE,{"disambiguationData":[OSD([sQuery(id+"F0.wireOp",EDGE,"E0.bottom")])],"isStart":true});
            var Q1;
            Q1=makeQuery(id+"F1.opExtrude","CAP_EDGE",EDGE,{"disambiguationData":[OSD([sQuery(id+"F0.wireOp",EDGE,"E0.left")])],"isStart":true});
            var Q2;
            Q2=makeQuery(id+"F1.opExtrude","CAP_EDGE",EDGE,{"disambiguationData":[OSD([sQuery(id+"F0.wireOp",EDGE,"E0.right")])],"isStart":true});
            var Q3;
            Q3=makeQuery(id+"F1.opExtrude","CAP_EDGE",EDGE,{"disambiguationData":[OSD([sQuery(id+"F0.wireOp",EDGE,"E0.top")])],"isStart":true});
            var Q4;
            Q4=makeQuery(id+"F1.opExtrude","CAP_EDGE",EDGE,{"disambiguationData":[OSD([sQuery(id+"F0.wireOp",EDGE,"E0.bottom")])],"isStart":false});
            var Q5;
            Q5=makeQuery(id+"F1.opExtrude","CAP_EDGE",EDGE,{"disambiguationData":[OSD([sQuery(id+"F0.wireOp",EDGE,"E0.left")])],"isStart":false});
            var Q6;
            Q6=makeQuery(id+"F1.opExtrude","CAP_EDGE",EDGE,{"disambiguationData":[OSD([sQuery(id+"F0.wireOp",EDGE,"E0.top")])],"isStart":false});
            var Q7;
            Q7=makeQuery(id+"F1.opExtrude","CAP_EDGE",EDGE,{"disambiguationData":[OSD([sQuery(id+"F0.wireOp",EDGE,"E0.right")])],"isStart":false});
            var Q8;
            Q8=makeQuery(id+"F1.opExtrude","SWEPT_EDGE",EDGE,{"disambiguationData":[OSD([sQuery(id+"F0.wireOp",EDGE,"E0.top"),sQuery(id+"F0.wireOp",EDGE,"E0.right")])]});
            var Q9;
            Q9=makeQuery(id+"F1.opExtrude","SWEPT_EDGE",EDGE,{"disambiguationData":[OSD([sQuery(id+"F0.wireOp",EDGE,"E0.bottom"),sQuery(id+"F0.wireOp",EDGE,"E0.right")])]});
            var Q10;
            Q10=makeQuery(id+"F1.opExtrude","SWEPT_EDGE",EDGE,{"disambiguationData":[OSD([sQuery(id+"F0.wireOp",EDGE,"E0.bottom"),sQuery(id+"F0.wireOp",EDGE,"E0.left")])]});
            var Q11;
            Q11=makeQuery(id+"F1.opExtrude","SWEPT_EDGE",EDGE,{"disambiguationData":[OSD([sQuery(id+"F0.wireOp",EDGE,"E0.top"),sQuery(id+"F0.wireOp",EDGE,"E0.left")])]});
            fillet(context, id + "F40", {"entities" : qUnion([Q0, Q1, Q2, Q3, Q4, Q5, Q6, Q7, Q8, Q9, Q10, Q11]), "radius" : 0.5 * mm, "tangentPropagation" : true, "allowEdgeOverflow" : false});
        }
    });
